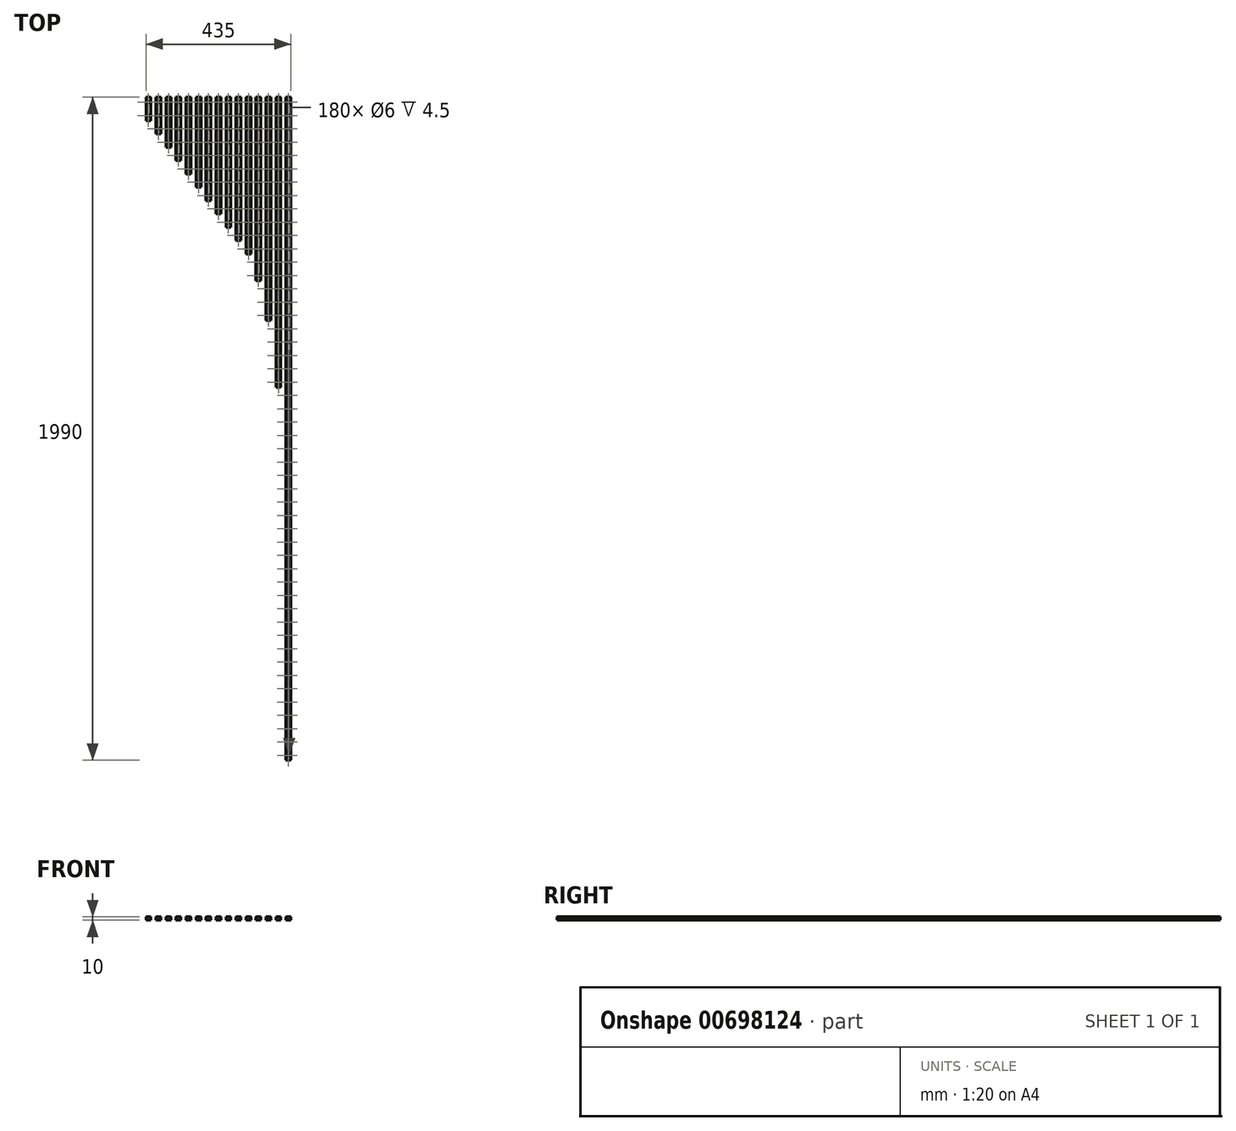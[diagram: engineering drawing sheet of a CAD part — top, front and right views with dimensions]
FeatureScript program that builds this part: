
annotation { "Feature Type Name" : "Feature", "Feature Type Description" : "" }
export const myFeature = defineFeature(function(context is Context, id is Id, definition is map)
    precondition{}
    {
        {
            var Q0;
            Q0=qCreatedBy(makeId("Front.planeOp"),FACE);
            var sketch = newSketch(context, id + "F0", { "sketchPlane" : qUnion([Q0])});
            skPoint(sketch, "E0.middle", {"position": v(0, 0) * mm});
            skLineSegment(sketch, "E1.bottom", {"start": v(6.8, -5) * mm, "end": v(-1.51, -5) * mm});
            skLineSegment(sketch, "E1.top", {"start": v(7, 5) * mm, "end": v(-7, 5) * mm});
            skLineSegment(sketch, "E1.left", {"start": v(7.5, -4.3) * mm, "end": v(7.5, 0.59) * mm});
            skLineSegment(sketch, "E1.right", {"start": v(-7.5, -4.3) * mm, "end": v(-7.5, 0.59) * mm});
            skArc(sketch, "E2", {"start": v(-7.5, 0.59) * mm, "mid": v(-6.98, 0.9) * mm, "end": v(-6.63, 1.4) * mm});
            skArc(sketch, "E3", {"start": v(7.5, 3.41) * mm, "mid": v(6.98, 3.1) * mm, "end": v(6.63, 2.6) * mm});
            skLineSegment(sketch, "E4", {"start": v(5.7, 2.6) * mm, "end": v(6.63, 2.6) * mm});
            skLineSegment(sketch, "E5", {"start": v(5.7, 1.4) * mm, "end": v(6.63, 1.4) * mm});
            skLineSegment(sketch, "E6", {"start": v(-5.7, 1.4) * mm, "end": v(-6.63, 1.4) * mm});
            skLineSegment(sketch, "E7", {"start": v(-5.7, 2.6) * mm, "end": v(-6.63, 2.6) * mm});
            skLineSegment(sketch, "E8", {"start": v(-7.5, 4.5) * mm, "end": v(-7, 5) * mm});
            skLineSegment(sketch, "E9.MirrorCS", {"start": v(7.5, 4.5) * mm, "end": v(7, 5) * mm});
            skLineSegment(sketch, "E10.MirrorCS", {"start": v(7.5, -4.3) * mm, "end": v(6.8, -5) * mm});
            skLineSegment(sketch, "E11.MirrorCS", {"start": v(-7.5, -4.3) * mm, "end": v(-6.8, -5) * mm});
            skPoint(sketch, "E12.orphan", {"position": v(-7.5, 5) * mm});
            skLineSegment(sketch, "E13.trimOffspring", {"start": v(-7.5, 3.41) * mm, "end": v(-7.5, 4.5) * mm});
            skArc(sketch, "E14.trimOffspring", {"start": v(-6.63, 2.6) * mm, "mid": v(-6.98, 3.1) * mm, "end": v(-7.5, 3.41) * mm});
            skPoint(sketch, "E15.orphan", {"position": v(7.5, 5) * mm});
            skLineSegment(sketch, "E16.trimOffspring", {"start": v(7.5, 3.41) * mm, "end": v(7.5, 4.5) * mm});
            skArc(sketch, "E17.trimOffspring", {"start": v(6.63, 1.4) * mm, "mid": v(6.98, 0.9) * mm, "end": v(7.5, 0.59) * mm});
            skPoint(sketch, "E18.orphan", {"position": v(7.5, -5) * mm});
            skPoint(sketch, "E19.orphan", {"position": v(-7.5, -5) * mm});
            skLineSegment(sketch, "E20", {"start": v(-5.7, 2.6) * mm, "end": v(-5.7, 1.4) * mm});
            skLineSegment(sketch, "E21", {"start": v(5.7, 2.6) * mm, "end": v(5.7, 1.4) * mm});
            skLineSegment(sketch, "E22", {"start": v(-8, 2) * mm, "end": v(8, 2) * mm, "construction": true});
            skArc(sketch, "E23", {"start": v(-1.51, -5) * mm, "mid": v(-2, -4.7) * mm, "end": v(-2.49, -5) * mm});
            skLineSegment(sketch, "E24.trimOffspring", {"start": v(-2.49, -5) * mm, "end": v(-6.8, -5) * mm});
            skLineSegment(sketch, "E25", {"start": v(-2.49, -5) * mm, "end": v(-1.51, -5) * mm, "construction": true});
            skLineSegment(sketch, "E26.1.0.0", {"start": v(37, 5) * mm, "end": v(23, 5) * mm});
            skLineSegment(sketch, "E26.1.0.1", {"start": v(36.8, -5) * mm, "end": v(28.49, -5) * mm});
            skArc(sketch, "E26.1.0.2", {"start": v(36.63, 1.4) * mm, "mid": v(36.98, 0.9) * mm, "end": v(37.5, 0.59) * mm});
            skPoint(sketch, "E26.1.0.3", {"position": v(37.5, -5) * mm});
            skPoint(sketch, "E26.1.0.4", {"position": v(22.5, -5) * mm});
            skLineSegment(sketch, "E26.1.0.5", {"start": v(37.5, -4.3) * mm, "end": v(37.5, 0.59) * mm});
            skPoint(sketch, "E26.1.0.6", {"position": v(22.5, 5) * mm});
            skPoint(sketch, "E26.1.0.7", {"position": v(30, 0) * mm});
            skLineSegment(sketch, "E26.1.0.8", {"start": v(22, 2) * mm, "end": v(38, 2) * mm, "construction": true});
            skLineSegment(sketch, "E26.1.0.9", {"start": v(27.51, -5) * mm, "end": v(23.2, -5) * mm});
            skLineSegment(sketch, "E26.1.0.10", {"start": v(22.5, -4.3) * mm, "end": v(22.5, 0.59) * mm});
            skArc(sketch, "E26.1.0.11", {"start": v(22.5, 0.59) * mm, "mid": v(23.02, 0.9) * mm, "end": v(23.37, 1.4) * mm});
            skPoint(sketch, "E26.1.0.12", {"position": v(37.5, 5) * mm});
            skPoint(sketch, "E26.1.0.13", {"position": v(30, 0) * mm});
            skArc(sketch, "E26.1.0.14", {"start": v(36.63, 1.4) * mm, "mid": v(36.98, 0.9) * mm, "end": v(37.5, 0.59) * mm});
            skLineSegment(sketch, "E26.1.0.15", {"start": v(22.5, 3.41) * mm, "end": v(22.5, 4.5) * mm});
            skLineSegment(sketch, "E26.1.0.16", {"start": v(35.7, 2.6) * mm, "end": v(35.7, 1.4) * mm});
            skLineSegment(sketch, "E26.1.0.17", {"start": v(37.5, 4.5) * mm, "end": v(37, 5) * mm});
            skLineSegment(sketch, "E26.1.0.18", {"start": v(37.5, 3.41) * mm, "end": v(37.5, 4.5) * mm});
            skArc(sketch, "E26.1.0.19", {"start": v(23.37, 2.6) * mm, "mid": v(23.02, 3.1) * mm, "end": v(22.5, 3.41) * mm});
            skLineSegment(sketch, "E26.1.0.20", {"start": v(22.5, 4.5) * mm, "end": v(23, 5) * mm});
            skLineSegment(sketch, "E26.1.0.21", {"start": v(22.5, -4.3) * mm, "end": v(23.2, -5) * mm});
            skLineSegment(sketch, "E26.1.0.22", {"start": v(24.3, 2.6) * mm, "end": v(23.37, 2.6) * mm});
            skLineSegment(sketch, "E26.1.0.23", {"start": v(37.5, -4.3) * mm, "end": v(36.8, -5) * mm});
            skLineSegment(sketch, "E26.1.0.24", {"start": v(24.3, 2.6) * mm, "end": v(24.3, 1.4) * mm});
            skArc(sketch, "E26.1.0.25", {"start": v(37.5, 3.41) * mm, "mid": v(36.98, 3.1) * mm, "end": v(36.63, 2.6) * mm});
            skLineSegment(sketch, "E26.1.0.26", {"start": v(35.7, 2.6) * mm, "end": v(36.63, 2.6) * mm});
            skLineSegment(sketch, "E26.1.0.27", {"start": v(35.7, 1.4) * mm, "end": v(36.63, 1.4) * mm});
            skLineSegment(sketch, "E26.1.0.28", {"start": v(24.3, 1.4) * mm, "end": v(23.37, 1.4) * mm});
            skArc(sketch, "E26.1.0.29", {"start": v(28.49, -5) * mm, "mid": v(28, -4.7) * mm, "end": v(27.51, -5) * mm});
            skLineSegment(sketch, "E26.1.0.30", {"start": v(27.51, -5) * mm, "end": v(28.49, -5) * mm, "construction": true});
            skLineSegment(sketch, "E26.2.0.0", {"start": v(67, 5) * mm, "end": v(53, 5) * mm});
            skLineSegment(sketch, "E26.2.0.1", {"start": v(66.8, -5) * mm, "end": v(58.49, -5) * mm});
            skArc(sketch, "E26.2.0.2", {"start": v(66.63, 1.4) * mm, "mid": v(66.98, 0.9) * mm, "end": v(67.5, 0.59) * mm});
            skPoint(sketch, "E26.2.0.3", {"position": v(67.5, -5) * mm});
            skPoint(sketch, "E26.2.0.4", {"position": v(52.5, -5) * mm});
            skLineSegment(sketch, "E26.2.0.5", {"start": v(67.5, -4.3) * mm, "end": v(67.5, 0.59) * mm});
            skPoint(sketch, "E26.2.0.6", {"position": v(52.5, 5) * mm});
            skPoint(sketch, "E26.2.0.7", {"position": v(60, 0) * mm});
            skLineSegment(sketch, "E26.2.0.8", {"start": v(52, 2) * mm, "end": v(68, 2) * mm, "construction": true});
            skLineSegment(sketch, "E26.2.0.9", {"start": v(57.51, -5) * mm, "end": v(53.2, -5) * mm});
            skLineSegment(sketch, "E26.2.0.10", {"start": v(52.5, -4.3) * mm, "end": v(52.5, 0.59) * mm});
            skArc(sketch, "E26.2.0.11", {"start": v(52.5, 0.59) * mm, "mid": v(53.02, 0.9) * mm, "end": v(53.37, 1.4) * mm});
            skPoint(sketch, "E26.2.0.12", {"position": v(67.5, 5) * mm});
            skPoint(sketch, "E26.2.0.13", {"position": v(60, 0) * mm});
            skArc(sketch, "E26.2.0.14", {"start": v(66.63, 1.4) * mm, "mid": v(66.98, 0.9) * mm, "end": v(67.5, 0.59) * mm});
            skLineSegment(sketch, "E26.2.0.15", {"start": v(52.5, 3.41) * mm, "end": v(52.5, 4.5) * mm});
            skLineSegment(sketch, "E26.2.0.16", {"start": v(65.7, 2.6) * mm, "end": v(65.7, 1.4) * mm});
            skLineSegment(sketch, "E26.2.0.17", {"start": v(67.5, 4.5) * mm, "end": v(67, 5) * mm});
            skLineSegment(sketch, "E26.2.0.18", {"start": v(67.5, 3.41) * mm, "end": v(67.5, 4.5) * mm});
            skArc(sketch, "E26.2.0.19", {"start": v(53.37, 2.6) * mm, "mid": v(53.02, 3.1) * mm, "end": v(52.5, 3.41) * mm});
            skLineSegment(sketch, "E26.2.0.20", {"start": v(52.5, 4.5) * mm, "end": v(53, 5) * mm});
            skLineSegment(sketch, "E26.2.0.21", {"start": v(52.5, -4.3) * mm, "end": v(53.2, -5) * mm});
            skLineSegment(sketch, "E26.2.0.22", {"start": v(54.3, 2.6) * mm, "end": v(53.37, 2.6) * mm});
            skLineSegment(sketch, "E26.2.0.23", {"start": v(67.5, -4.3) * mm, "end": v(66.8, -5) * mm});
            skLineSegment(sketch, "E26.2.0.24", {"start": v(54.3, 2.6) * mm, "end": v(54.3, 1.4) * mm});
            skArc(sketch, "E26.2.0.25", {"start": v(67.5, 3.41) * mm, "mid": v(66.98, 3.1) * mm, "end": v(66.63, 2.6) * mm});
            skLineSegment(sketch, "E26.2.0.26", {"start": v(65.7, 2.6) * mm, "end": v(66.63, 2.6) * mm});
            skLineSegment(sketch, "E26.2.0.27", {"start": v(65.7, 1.4) * mm, "end": v(66.63, 1.4) * mm});
            skLineSegment(sketch, "E26.2.0.28", {"start": v(54.3, 1.4) * mm, "end": v(53.37, 1.4) * mm});
            skArc(sketch, "E26.2.0.29", {"start": v(58.49, -5) * mm, "mid": v(58, -4.7) * mm, "end": v(57.51, -5) * mm});
            skLineSegment(sketch, "E26.2.0.30", {"start": v(57.51, -5) * mm, "end": v(58.49, -5) * mm, "construction": true});
            skLineSegment(sketch, "E26.3.0.0", {"start": v(97, 5) * mm, "end": v(83, 5) * mm});
            skLineSegment(sketch, "E26.3.0.1", {"start": v(96.8, -5) * mm, "end": v(88.49, -5) * mm});
            skArc(sketch, "E26.3.0.2", {"start": v(96.63, 1.4) * mm, "mid": v(96.98, 0.9) * mm, "end": v(97.5, 0.59) * mm});
            skPoint(sketch, "E26.3.0.3", {"position": v(97.5, -5) * mm});
            skPoint(sketch, "E26.3.0.4", {"position": v(82.5, -5) * mm});
            skLineSegment(sketch, "E26.3.0.5", {"start": v(97.5, -4.3) * mm, "end": v(97.5, 0.59) * mm});
            skPoint(sketch, "E26.3.0.6", {"position": v(82.5, 5) * mm});
            skPoint(sketch, "E26.3.0.7", {"position": v(90, 0) * mm});
            skLineSegment(sketch, "E26.3.0.8", {"start": v(82, 2) * mm, "end": v(98, 2) * mm, "construction": true});
            skLineSegment(sketch, "E26.3.0.9", {"start": v(87.51, -5) * mm, "end": v(83.2, -5) * mm});
            skLineSegment(sketch, "E26.3.0.10", {"start": v(82.5, -4.3) * mm, "end": v(82.5, 0.59) * mm});
            skArc(sketch, "E26.3.0.11", {"start": v(82.5, 0.59) * mm, "mid": v(83.02, 0.9) * mm, "end": v(83.37, 1.4) * mm});
            skPoint(sketch, "E26.3.0.12", {"position": v(97.5, 5) * mm});
            skPoint(sketch, "E26.3.0.13", {"position": v(90, 0) * mm});
            skArc(sketch, "E26.3.0.14", {"start": v(96.63, 1.4) * mm, "mid": v(96.98, 0.9) * mm, "end": v(97.5, 0.59) * mm});
            skLineSegment(sketch, "E26.3.0.15", {"start": v(82.5, 3.41) * mm, "end": v(82.5, 4.5) * mm});
            skLineSegment(sketch, "E26.3.0.16", {"start": v(95.7, 2.6) * mm, "end": v(95.7, 1.4) * mm});
            skLineSegment(sketch, "E26.3.0.17", {"start": v(97.5, 4.5) * mm, "end": v(97, 5) * mm});
            skLineSegment(sketch, "E26.3.0.18", {"start": v(97.5, 3.41) * mm, "end": v(97.5, 4.5) * mm});
            skArc(sketch, "E26.3.0.19", {"start": v(83.37, 2.6) * mm, "mid": v(83.02, 3.1) * mm, "end": v(82.5, 3.41) * mm});
            skLineSegment(sketch, "E26.3.0.20", {"start": v(82.5, 4.5) * mm, "end": v(83, 5) * mm});
            skLineSegment(sketch, "E26.3.0.21", {"start": v(82.5, -4.3) * mm, "end": v(83.2, -5) * mm});
            skLineSegment(sketch, "E26.3.0.22", {"start": v(84.3, 2.6) * mm, "end": v(83.37, 2.6) * mm});
            skLineSegment(sketch, "E26.3.0.23", {"start": v(97.5, -4.3) * mm, "end": v(96.8, -5) * mm});
            skLineSegment(sketch, "E26.3.0.24", {"start": v(84.3, 2.6) * mm, "end": v(84.3, 1.4) * mm});
            skArc(sketch, "E26.3.0.25", {"start": v(97.5, 3.41) * mm, "mid": v(96.98, 3.1) * mm, "end": v(96.63, 2.6) * mm});
            skLineSegment(sketch, "E26.3.0.26", {"start": v(95.7, 2.6) * mm, "end": v(96.63, 2.6) * mm});
            skLineSegment(sketch, "E26.3.0.27", {"start": v(95.7, 1.4) * mm, "end": v(96.63, 1.4) * mm});
            skLineSegment(sketch, "E26.3.0.28", {"start": v(84.3, 1.4) * mm, "end": v(83.37, 1.4) * mm});
            skArc(sketch, "E26.3.0.29", {"start": v(88.49, -5) * mm, "mid": v(88, -4.7) * mm, "end": v(87.51, -5) * mm});
            skLineSegment(sketch, "E26.3.0.30", {"start": v(87.51, -5) * mm, "end": v(88.49, -5) * mm, "construction": true});
            skLineSegment(sketch, "E26.4.0.0", {"start": v(127, 5) * mm, "end": v(113, 5) * mm});
            skLineSegment(sketch, "E26.4.0.1", {"start": v(126.8, -5) * mm, "end": v(118.49, -5) * mm});
            skArc(sketch, "E26.4.0.2", {"start": v(126.63, 1.4) * mm, "mid": v(126.98, 0.9) * mm, "end": v(127.5, 0.59) * mm});
            skPoint(sketch, "E26.4.0.3", {"position": v(127.5, -5) * mm});
            skPoint(sketch, "E26.4.0.4", {"position": v(112.5, -5) * mm});
            skLineSegment(sketch, "E26.4.0.5", {"start": v(127.5, -4.3) * mm, "end": v(127.5, 0.59) * mm});
            skPoint(sketch, "E26.4.0.6", {"position": v(112.5, 5) * mm});
            skPoint(sketch, "E26.4.0.7", {"position": v(120, 0) * mm});
            skLineSegment(sketch, "E26.4.0.8", {"start": v(112, 2) * mm, "end": v(128, 2) * mm, "construction": true});
            skLineSegment(sketch, "E26.4.0.9", {"start": v(117.51, -5) * mm, "end": v(113.2, -5) * mm});
            skLineSegment(sketch, "E26.4.0.10", {"start": v(112.5, -4.3) * mm, "end": v(112.5, 0.59) * mm});
            skArc(sketch, "E26.4.0.11", {"start": v(112.5, 0.59) * mm, "mid": v(113.02, 0.9) * mm, "end": v(113.37, 1.4) * mm});
            skPoint(sketch, "E26.4.0.12", {"position": v(127.5, 5) * mm});
            skPoint(sketch, "E26.4.0.13", {"position": v(120, 0) * mm});
            skArc(sketch, "E26.4.0.14", {"start": v(126.63, 1.4) * mm, "mid": v(126.98, 0.9) * mm, "end": v(127.5, 0.59) * mm});
            skLineSegment(sketch, "E26.4.0.15", {"start": v(112.5, 3.41) * mm, "end": v(112.5, 4.5) * mm});
            skLineSegment(sketch, "E26.4.0.16", {"start": v(125.7, 2.6) * mm, "end": v(125.7, 1.4) * mm});
            skLineSegment(sketch, "E26.4.0.17", {"start": v(127.5, 4.5) * mm, "end": v(127, 5) * mm});
            skLineSegment(sketch, "E26.4.0.18", {"start": v(127.5, 3.41) * mm, "end": v(127.5, 4.5) * mm});
            skArc(sketch, "E26.4.0.19", {"start": v(113.37, 2.6) * mm, "mid": v(113.02, 3.1) * mm, "end": v(112.5, 3.41) * mm});
            skLineSegment(sketch, "E26.4.0.20", {"start": v(112.5, 4.5) * mm, "end": v(113, 5) * mm});
            skLineSegment(sketch, "E26.4.0.21", {"start": v(112.5, -4.3) * mm, "end": v(113.2, -5) * mm});
            skLineSegment(sketch, "E26.4.0.22", {"start": v(114.3, 2.6) * mm, "end": v(113.37, 2.6) * mm});
            skLineSegment(sketch, "E26.4.0.23", {"start": v(127.5, -4.3) * mm, "end": v(126.8, -5) * mm});
            skLineSegment(sketch, "E26.4.0.24", {"start": v(114.3, 2.6) * mm, "end": v(114.3, 1.4) * mm});
            skArc(sketch, "E26.4.0.25", {"start": v(127.5, 3.41) * mm, "mid": v(126.98, 3.1) * mm, "end": v(126.63, 2.6) * mm});
            skLineSegment(sketch, "E26.4.0.26", {"start": v(125.7, 2.6) * mm, "end": v(126.63, 2.6) * mm});
            skLineSegment(sketch, "E26.4.0.27", {"start": v(125.7, 1.4) * mm, "end": v(126.63, 1.4) * mm});
            skLineSegment(sketch, "E26.4.0.28", {"start": v(114.3, 1.4) * mm, "end": v(113.37, 1.4) * mm});
            skArc(sketch, "E26.4.0.29", {"start": v(118.49, -5) * mm, "mid": v(118, -4.7) * mm, "end": v(117.51, -5) * mm});
            skLineSegment(sketch, "E26.4.0.30", {"start": v(117.51, -5) * mm, "end": v(118.49, -5) * mm, "construction": true});
            skLineSegment(sketch, "E26.5.0.0", {"start": v(157, 5) * mm, "end": v(143, 5) * mm});
            skLineSegment(sketch, "E26.5.0.1", {"start": v(156.8, -5) * mm, "end": v(148.49, -5) * mm});
            skArc(sketch, "E26.5.0.2", {"start": v(156.63, 1.4) * mm, "mid": v(156.98, 0.9) * mm, "end": v(157.5, 0.59) * mm});
            skPoint(sketch, "E26.5.0.3", {"position": v(157.5, -5) * mm});
            skPoint(sketch, "E26.5.0.4", {"position": v(142.5, -5) * mm});
            skLineSegment(sketch, "E26.5.0.5", {"start": v(157.5, -4.3) * mm, "end": v(157.5, 0.59) * mm});
            skPoint(sketch, "E26.5.0.6", {"position": v(142.5, 5) * mm});
            skPoint(sketch, "E26.5.0.7", {"position": v(150, 0) * mm});
            skLineSegment(sketch, "E26.5.0.8", {"start": v(142, 2) * mm, "end": v(158, 2) * mm, "construction": true});
            skLineSegment(sketch, "E26.5.0.9", {"start": v(147.51, -5) * mm, "end": v(143.2, -5) * mm});
            skLineSegment(sketch, "E26.5.0.10", {"start": v(142.5, -4.3) * mm, "end": v(142.5, 0.59) * mm});
            skArc(sketch, "E26.5.0.11", {"start": v(142.5, 0.59) * mm, "mid": v(143.02, 0.9) * mm, "end": v(143.37, 1.4) * mm});
            skPoint(sketch, "E26.5.0.12", {"position": v(157.5, 5) * mm});
            skPoint(sketch, "E26.5.0.13", {"position": v(150, 0) * mm});
            skArc(sketch, "E26.5.0.14", {"start": v(156.63, 1.4) * mm, "mid": v(156.98, 0.9) * mm, "end": v(157.5, 0.59) * mm});
            skLineSegment(sketch, "E26.5.0.15", {"start": v(142.5, 3.41) * mm, "end": v(142.5, 4.5) * mm});
            skLineSegment(sketch, "E26.5.0.16", {"start": v(155.7, 2.6) * mm, "end": v(155.7, 1.4) * mm});
            skLineSegment(sketch, "E26.5.0.17", {"start": v(157.5, 4.5) * mm, "end": v(157, 5) * mm});
            skLineSegment(sketch, "E26.5.0.18", {"start": v(157.5, 3.41) * mm, "end": v(157.5, 4.5) * mm});
            skArc(sketch, "E26.5.0.19", {"start": v(143.37, 2.6) * mm, "mid": v(143.02, 3.1) * mm, "end": v(142.5, 3.41) * mm});
            skLineSegment(sketch, "E26.5.0.20", {"start": v(142.5, 4.5) * mm, "end": v(143, 5) * mm});
            skLineSegment(sketch, "E26.5.0.21", {"start": v(142.5, -4.3) * mm, "end": v(143.2, -5) * mm});
            skLineSegment(sketch, "E26.5.0.22", {"start": v(144.3, 2.6) * mm, "end": v(143.37, 2.6) * mm});
            skLineSegment(sketch, "E26.5.0.23", {"start": v(157.5, -4.3) * mm, "end": v(156.8, -5) * mm});
            skLineSegment(sketch, "E26.5.0.24", {"start": v(144.3, 2.6) * mm, "end": v(144.3, 1.4) * mm});
            skArc(sketch, "E26.5.0.25", {"start": v(157.5, 3.41) * mm, "mid": v(156.98, 3.1) * mm, "end": v(156.63, 2.6) * mm});
            skLineSegment(sketch, "E26.5.0.26", {"start": v(155.7, 2.6) * mm, "end": v(156.63, 2.6) * mm});
            skLineSegment(sketch, "E26.5.0.27", {"start": v(155.7, 1.4) * mm, "end": v(156.63, 1.4) * mm});
            skLineSegment(sketch, "E26.5.0.28", {"start": v(144.3, 1.4) * mm, "end": v(143.37, 1.4) * mm});
            skArc(sketch, "E26.5.0.29", {"start": v(148.49, -5) * mm, "mid": v(148, -4.7) * mm, "end": v(147.51, -5) * mm});
            skLineSegment(sketch, "E26.5.0.30", {"start": v(147.51, -5) * mm, "end": v(148.49, -5) * mm, "construction": true});
            skLineSegment(sketch, "E26.6.0.0", {"start": v(187, 5) * mm, "end": v(173, 5) * mm});
            skLineSegment(sketch, "E26.6.0.1", {"start": v(186.8, -5) * mm, "end": v(178.49, -5) * mm});
            skArc(sketch, "E26.6.0.2", {"start": v(186.63, 1.4) * mm, "mid": v(186.98, 0.9) * mm, "end": v(187.5, 0.59) * mm});
            skPoint(sketch, "E26.6.0.3", {"position": v(187.5, -5) * mm});
            skPoint(sketch, "E26.6.0.4", {"position": v(172.5, -5) * mm});
            skLineSegment(sketch, "E26.6.0.5", {"start": v(187.5, -4.3) * mm, "end": v(187.5, 0.59) * mm});
            skPoint(sketch, "E26.6.0.6", {"position": v(172.5, 5) * mm});
            skPoint(sketch, "E26.6.0.7", {"position": v(180, 0) * mm});
            skLineSegment(sketch, "E26.6.0.8", {"start": v(172, 2) * mm, "end": v(188, 2) * mm, "construction": true});
            skLineSegment(sketch, "E26.6.0.9", {"start": v(177.51, -5) * mm, "end": v(173.2, -5) * mm});
            skLineSegment(sketch, "E26.6.0.10", {"start": v(172.5, -4.3) * mm, "end": v(172.5, 0.59) * mm});
            skArc(sketch, "E26.6.0.11", {"start": v(172.5, 0.59) * mm, "mid": v(173.02, 0.9) * mm, "end": v(173.37, 1.4) * mm});
            skPoint(sketch, "E26.6.0.12", {"position": v(187.5, 5) * mm});
            skPoint(sketch, "E26.6.0.13", {"position": v(180, 0) * mm});
            skArc(sketch, "E26.6.0.14", {"start": v(186.63, 1.4) * mm, "mid": v(186.98, 0.9) * mm, "end": v(187.5, 0.59) * mm});
            skLineSegment(sketch, "E26.6.0.15", {"start": v(172.5, 3.41) * mm, "end": v(172.5, 4.5) * mm});
            skLineSegment(sketch, "E26.6.0.16", {"start": v(185.7, 2.6) * mm, "end": v(185.7, 1.4) * mm});
            skLineSegment(sketch, "E26.6.0.17", {"start": v(187.5, 4.5) * mm, "end": v(187, 5) * mm});
            skLineSegment(sketch, "E26.6.0.18", {"start": v(187.5, 3.41) * mm, "end": v(187.5, 4.5) * mm});
            skArc(sketch, "E26.6.0.19", {"start": v(173.37, 2.6) * mm, "mid": v(173.02, 3.1) * mm, "end": v(172.5, 3.41) * mm});
            skLineSegment(sketch, "E26.6.0.20", {"start": v(172.5, 4.5) * mm, "end": v(173, 5) * mm});
            skLineSegment(sketch, "E26.6.0.21", {"start": v(172.5, -4.3) * mm, "end": v(173.2, -5) * mm});
            skLineSegment(sketch, "E26.6.0.22", {"start": v(174.3, 2.6) * mm, "end": v(173.37, 2.6) * mm});
            skLineSegment(sketch, "E26.6.0.23", {"start": v(187.5, -4.3) * mm, "end": v(186.8, -5) * mm});
            skLineSegment(sketch, "E26.6.0.24", {"start": v(174.3, 2.6) * mm, "end": v(174.3, 1.4) * mm});
            skArc(sketch, "E26.6.0.25", {"start": v(187.5, 3.41) * mm, "mid": v(186.98, 3.1) * mm, "end": v(186.63, 2.6) * mm});
            skLineSegment(sketch, "E26.6.0.26", {"start": v(185.7, 2.6) * mm, "end": v(186.63, 2.6) * mm});
            skLineSegment(sketch, "E26.6.0.27", {"start": v(185.7, 1.4) * mm, "end": v(186.63, 1.4) * mm});
            skLineSegment(sketch, "E26.6.0.28", {"start": v(174.3, 1.4) * mm, "end": v(173.37, 1.4) * mm});
            skArc(sketch, "E26.6.0.29", {"start": v(178.49, -5) * mm, "mid": v(178, -4.7) * mm, "end": v(177.51, -5) * mm});
            skLineSegment(sketch, "E26.6.0.30", {"start": v(177.51, -5) * mm, "end": v(178.49, -5) * mm, "construction": true});
            skLineSegment(sketch, "E26.7.0.0", {"start": v(217, 5) * mm, "end": v(203, 5) * mm});
            skLineSegment(sketch, "E26.7.0.1", {"start": v(216.8, -5) * mm, "end": v(208.49, -5) * mm});
            skArc(sketch, "E26.7.0.2", {"start": v(216.63, 1.4) * mm, "mid": v(216.98, 0.9) * mm, "end": v(217.5, 0.59) * mm});
            skPoint(sketch, "E26.7.0.3", {"position": v(217.5, -5) * mm});
            skPoint(sketch, "E26.7.0.4", {"position": v(202.5, -5) * mm});
            skLineSegment(sketch, "E26.7.0.5", {"start": v(217.5, -4.3) * mm, "end": v(217.5, 0.59) * mm});
            skPoint(sketch, "E26.7.0.6", {"position": v(202.5, 5) * mm});
            skPoint(sketch, "E26.7.0.7", {"position": v(210, 0) * mm});
            skLineSegment(sketch, "E26.7.0.8", {"start": v(202, 2) * mm, "end": v(218, 2) * mm, "construction": true});
            skLineSegment(sketch, "E26.7.0.9", {"start": v(207.51, -5) * mm, "end": v(203.2, -5) * mm});
            skLineSegment(sketch, "E26.7.0.10", {"start": v(202.5, -4.3) * mm, "end": v(202.5, 0.59) * mm});
            skArc(sketch, "E26.7.0.11", {"start": v(202.5, 0.59) * mm, "mid": v(203.02, 0.9) * mm, "end": v(203.37, 1.4) * mm});
            skPoint(sketch, "E26.7.0.12", {"position": v(217.5, 5) * mm});
            skPoint(sketch, "E26.7.0.13", {"position": v(210, 0) * mm});
            skArc(sketch, "E26.7.0.14", {"start": v(216.63, 1.4) * mm, "mid": v(216.98, 0.9) * mm, "end": v(217.5, 0.59) * mm});
            skLineSegment(sketch, "E26.7.0.15", {"start": v(202.5, 3.41) * mm, "end": v(202.5, 4.5) * mm});
            skLineSegment(sketch, "E26.7.0.16", {"start": v(215.7, 2.6) * mm, "end": v(215.7, 1.4) * mm});
            skLineSegment(sketch, "E26.7.0.17", {"start": v(217.5, 4.5) * mm, "end": v(217, 5) * mm});
            skLineSegment(sketch, "E26.7.0.18", {"start": v(217.5, 3.41) * mm, "end": v(217.5, 4.5) * mm});
            skArc(sketch, "E26.7.0.19", {"start": v(203.37, 2.6) * mm, "mid": v(203.02, 3.1) * mm, "end": v(202.5, 3.41) * mm});
            skLineSegment(sketch, "E26.7.0.20", {"start": v(202.5, 4.5) * mm, "end": v(203, 5) * mm});
            skLineSegment(sketch, "E26.7.0.21", {"start": v(202.5, -4.3) * mm, "end": v(203.2, -5) * mm});
            skLineSegment(sketch, "E26.7.0.22", {"start": v(204.3, 2.6) * mm, "end": v(203.37, 2.6) * mm});
            skLineSegment(sketch, "E26.7.0.23", {"start": v(217.5, -4.3) * mm, "end": v(216.8, -5) * mm});
            skLineSegment(sketch, "E26.7.0.24", {"start": v(204.3, 2.6) * mm, "end": v(204.3, 1.4) * mm});
            skArc(sketch, "E26.7.0.25", {"start": v(217.5, 3.41) * mm, "mid": v(216.98, 3.1) * mm, "end": v(216.63, 2.6) * mm});
            skLineSegment(sketch, "E26.7.0.26", {"start": v(215.7, 2.6) * mm, "end": v(216.63, 2.6) * mm});
            skLineSegment(sketch, "E26.7.0.27", {"start": v(215.7, 1.4) * mm, "end": v(216.63, 1.4) * mm});
            skLineSegment(sketch, "E26.7.0.28", {"start": v(204.3, 1.4) * mm, "end": v(203.37, 1.4) * mm});
            skArc(sketch, "E26.7.0.29", {"start": v(208.49, -5) * mm, "mid": v(208, -4.7) * mm, "end": v(207.51, -5) * mm});
            skLineSegment(sketch, "E26.7.0.30", {"start": v(207.51, -5) * mm, "end": v(208.49, -5) * mm, "construction": true});
            skLineSegment(sketch, "E26.8.0.0", {"start": v(247, 5) * mm, "end": v(233, 5) * mm});
            skLineSegment(sketch, "E26.8.0.1", {"start": v(246.8, -5) * mm, "end": v(238.49, -5) * mm});
            skArc(sketch, "E26.8.0.2", {"start": v(246.63, 1.4) * mm, "mid": v(246.98, 0.9) * mm, "end": v(247.5, 0.59) * mm});
            skPoint(sketch, "E26.8.0.3", {"position": v(247.5, -5) * mm});
            skPoint(sketch, "E26.8.0.4", {"position": v(232.5, -5) * mm});
            skLineSegment(sketch, "E26.8.0.5", {"start": v(247.5, -4.3) * mm, "end": v(247.5, 0.59) * mm});
            skPoint(sketch, "E26.8.0.6", {"position": v(232.5, 5) * mm});
            skPoint(sketch, "E26.8.0.7", {"position": v(240, 0) * mm});
            skLineSegment(sketch, "E26.8.0.8", {"start": v(232, 2) * mm, "end": v(248, 2) * mm, "construction": true});
            skLineSegment(sketch, "E26.8.0.9", {"start": v(237.51, -5) * mm, "end": v(233.2, -5) * mm});
            skLineSegment(sketch, "E26.8.0.10", {"start": v(232.5, -4.3) * mm, "end": v(232.5, 0.59) * mm});
            skArc(sketch, "E26.8.0.11", {"start": v(232.5, 0.59) * mm, "mid": v(233.02, 0.9) * mm, "end": v(233.37, 1.4) * mm});
            skPoint(sketch, "E26.8.0.12", {"position": v(247.5, 5) * mm});
            skPoint(sketch, "E26.8.0.13", {"position": v(240, 0) * mm});
            skArc(sketch, "E26.8.0.14", {"start": v(246.63, 1.4) * mm, "mid": v(246.98, 0.9) * mm, "end": v(247.5, 0.59) * mm});
            skLineSegment(sketch, "E26.8.0.15", {"start": v(232.5, 3.41) * mm, "end": v(232.5, 4.5) * mm});
            skLineSegment(sketch, "E26.8.0.16", {"start": v(245.7, 2.6) * mm, "end": v(245.7, 1.4) * mm});
            skLineSegment(sketch, "E26.8.0.17", {"start": v(247.5, 4.5) * mm, "end": v(247, 5) * mm});
            skLineSegment(sketch, "E26.8.0.18", {"start": v(247.5, 3.41) * mm, "end": v(247.5, 4.5) * mm});
            skArc(sketch, "E26.8.0.19", {"start": v(233.37, 2.6) * mm, "mid": v(233.02, 3.1) * mm, "end": v(232.5, 3.41) * mm});
            skLineSegment(sketch, "E26.8.0.20", {"start": v(232.5, 4.5) * mm, "end": v(233, 5) * mm});
            skLineSegment(sketch, "E26.8.0.21", {"start": v(232.5, -4.3) * mm, "end": v(233.2, -5) * mm});
            skLineSegment(sketch, "E26.8.0.22", {"start": v(234.3, 2.6) * mm, "end": v(233.37, 2.6) * mm});
            skLineSegment(sketch, "E26.8.0.23", {"start": v(247.5, -4.3) * mm, "end": v(246.8, -5) * mm});
            skLineSegment(sketch, "E26.8.0.24", {"start": v(234.3, 2.6) * mm, "end": v(234.3, 1.4) * mm});
            skArc(sketch, "E26.8.0.25", {"start": v(247.5, 3.41) * mm, "mid": v(246.98, 3.1) * mm, "end": v(246.63, 2.6) * mm});
            skLineSegment(sketch, "E26.8.0.26", {"start": v(245.7, 2.6) * mm, "end": v(246.63, 2.6) * mm});
            skLineSegment(sketch, "E26.8.0.27", {"start": v(245.7, 1.4) * mm, "end": v(246.63, 1.4) * mm});
            skLineSegment(sketch, "E26.8.0.28", {"start": v(234.3, 1.4) * mm, "end": v(233.37, 1.4) * mm});
            skArc(sketch, "E26.8.0.29", {"start": v(238.49, -5) * mm, "mid": v(238, -4.7) * mm, "end": v(237.51, -5) * mm});
            skLineSegment(sketch, "E26.8.0.30", {"start": v(237.51, -5) * mm, "end": v(238.49, -5) * mm, "construction": true});
            skLineSegment(sketch, "E26.9.0.0", {"start": v(277, 5) * mm, "end": v(263, 5) * mm});
            skLineSegment(sketch, "E26.9.0.1", {"start": v(276.8, -5) * mm, "end": v(268.49, -5) * mm});
            skArc(sketch, "E26.9.0.2", {"start": v(276.63, 1.4) * mm, "mid": v(276.98, 0.9) * mm, "end": v(277.5, 0.59) * mm});
            skPoint(sketch, "E26.9.0.3", {"position": v(277.5, -5) * mm});
            skPoint(sketch, "E26.9.0.4", {"position": v(262.5, -5) * mm});
            skLineSegment(sketch, "E26.9.0.5", {"start": v(277.5, -4.3) * mm, "end": v(277.5, 0.59) * mm});
            skPoint(sketch, "E26.9.0.6", {"position": v(262.5, 5) * mm});
            skPoint(sketch, "E26.9.0.7", {"position": v(270, 0) * mm});
            skLineSegment(sketch, "E26.9.0.8", {"start": v(262, 2) * mm, "end": v(278, 2) * mm, "construction": true});
            skLineSegment(sketch, "E26.9.0.9", {"start": v(267.51, -5) * mm, "end": v(263.2, -5) * mm});
            skLineSegment(sketch, "E26.9.0.10", {"start": v(262.5, -4.3) * mm, "end": v(262.5, 0.59) * mm});
            skArc(sketch, "E26.9.0.11", {"start": v(262.5, 0.59) * mm, "mid": v(263.02, 0.9) * mm, "end": v(263.37, 1.4) * mm});
            skPoint(sketch, "E26.9.0.12", {"position": v(277.5, 5) * mm});
            skPoint(sketch, "E26.9.0.13", {"position": v(270, 0) * mm});
            skArc(sketch, "E26.9.0.14", {"start": v(276.63, 1.4) * mm, "mid": v(276.98, 0.9) * mm, "end": v(277.5, 0.59) * mm});
            skLineSegment(sketch, "E26.9.0.15", {"start": v(262.5, 3.41) * mm, "end": v(262.5, 4.5) * mm});
            skLineSegment(sketch, "E26.9.0.16", {"start": v(275.7, 2.6) * mm, "end": v(275.7, 1.4) * mm});
            skLineSegment(sketch, "E26.9.0.17", {"start": v(277.5, 4.5) * mm, "end": v(277, 5) * mm});
            skLineSegment(sketch, "E26.9.0.18", {"start": v(277.5, 3.41) * mm, "end": v(277.5, 4.5) * mm});
            skArc(sketch, "E26.9.0.19", {"start": v(263.37, 2.6) * mm, "mid": v(263.02, 3.1) * mm, "end": v(262.5, 3.41) * mm});
            skLineSegment(sketch, "E26.9.0.20", {"start": v(262.5, 4.5) * mm, "end": v(263, 5) * mm});
            skLineSegment(sketch, "E26.9.0.21", {"start": v(262.5, -4.3) * mm, "end": v(263.2, -5) * mm});
            skLineSegment(sketch, "E26.9.0.22", {"start": v(264.3, 2.6) * mm, "end": v(263.37, 2.6) * mm});
            skLineSegment(sketch, "E26.9.0.23", {"start": v(277.5, -4.3) * mm, "end": v(276.8, -5) * mm});
            skLineSegment(sketch, "E26.9.0.24", {"start": v(264.3, 2.6) * mm, "end": v(264.3, 1.4) * mm});
            skArc(sketch, "E26.9.0.25", {"start": v(277.5, 3.41) * mm, "mid": v(276.98, 3.1) * mm, "end": v(276.63, 2.6) * mm});
            skLineSegment(sketch, "E26.9.0.26", {"start": v(275.7, 2.6) * mm, "end": v(276.63, 2.6) * mm});
            skLineSegment(sketch, "E26.9.0.27", {"start": v(275.7, 1.4) * mm, "end": v(276.63, 1.4) * mm});
            skLineSegment(sketch, "E26.9.0.28", {"start": v(264.3, 1.4) * mm, "end": v(263.37, 1.4) * mm});
            skArc(sketch, "E26.9.0.29", {"start": v(268.49, -5) * mm, "mid": v(268, -4.7) * mm, "end": v(267.51, -5) * mm});
            skLineSegment(sketch, "E26.9.0.30", {"start": v(267.51, -5) * mm, "end": v(268.49, -5) * mm, "construction": true});
            skLineSegment(sketch, "E26.10.0.0", {"start": v(307, 5) * mm, "end": v(293, 5) * mm});
            skLineSegment(sketch, "E26.10.0.1", {"start": v(306.8, -5) * mm, "end": v(298.49, -5) * mm});
            skArc(sketch, "E26.10.0.2", {"start": v(306.63, 1.4) * mm, "mid": v(306.98, 0.9) * mm, "end": v(307.5, 0.59) * mm});
            skPoint(sketch, "E26.10.0.3", {"position": v(307.5, -5) * mm});
            skPoint(sketch, "E26.10.0.4", {"position": v(292.5, -5) * mm});
            skLineSegment(sketch, "E26.10.0.5", {"start": v(307.5, -4.3) * mm, "end": v(307.5, 0.59) * mm});
            skPoint(sketch, "E26.10.0.6", {"position": v(292.5, 5) * mm});
            skPoint(sketch, "E26.10.0.7", {"position": v(300, 0) * mm});
            skLineSegment(sketch, "E26.10.0.8", {"start": v(292, 2) * mm, "end": v(308, 2) * mm, "construction": true});
            skLineSegment(sketch, "E26.10.0.9", {"start": v(297.51, -5) * mm, "end": v(293.2, -5) * mm});
            skLineSegment(sketch, "E26.10.0.10", {"start": v(292.5, -4.3) * mm, "end": v(292.5, 0.59) * mm});
            skArc(sketch, "E26.10.0.11", {"start": v(292.5, 0.59) * mm, "mid": v(293.02, 0.9) * mm, "end": v(293.37, 1.4) * mm});
            skPoint(sketch, "E26.10.0.12", {"position": v(307.5, 5) * mm});
            skPoint(sketch, "E26.10.0.13", {"position": v(300, 0) * mm});
            skArc(sketch, "E26.10.0.14", {"start": v(306.63, 1.4) * mm, "mid": v(306.98, 0.9) * mm, "end": v(307.5, 0.59) * mm});
            skLineSegment(sketch, "E26.10.0.15", {"start": v(292.5, 3.41) * mm, "end": v(292.5, 4.5) * mm});
            skLineSegment(sketch, "E26.10.0.16", {"start": v(305.7, 2.6) * mm, "end": v(305.7, 1.4) * mm});
            skLineSegment(sketch, "E26.10.0.17", {"start": v(307.5, 4.5) * mm, "end": v(307, 5) * mm});
            skLineSegment(sketch, "E26.10.0.18", {"start": v(307.5, 3.41) * mm, "end": v(307.5, 4.5) * mm});
            skArc(sketch, "E26.10.0.19", {"start": v(293.37, 2.6) * mm, "mid": v(293.02, 3.1) * mm, "end": v(292.5, 3.41) * mm});
            skLineSegment(sketch, "E26.10.0.20", {"start": v(292.5, 4.5) * mm, "end": v(293, 5) * mm});
            skLineSegment(sketch, "E26.10.0.21", {"start": v(292.5, -4.3) * mm, "end": v(293.2, -5) * mm});
            skLineSegment(sketch, "E26.10.0.22", {"start": v(294.3, 2.6) * mm, "end": v(293.37, 2.6) * mm});
            skLineSegment(sketch, "E26.10.0.23", {"start": v(307.5, -4.3) * mm, "end": v(306.8, -5) * mm});
            skLineSegment(sketch, "E26.10.0.24", {"start": v(294.3, 2.6) * mm, "end": v(294.3, 1.4) * mm});
            skArc(sketch, "E26.10.0.25", {"start": v(307.5, 3.41) * mm, "mid": v(306.98, 3.1) * mm, "end": v(306.63, 2.6) * mm});
            skLineSegment(sketch, "E26.10.0.26", {"start": v(305.7, 2.6) * mm, "end": v(306.63, 2.6) * mm});
            skLineSegment(sketch, "E26.10.0.27", {"start": v(305.7, 1.4) * mm, "end": v(306.63, 1.4) * mm});
            skLineSegment(sketch, "E26.10.0.28", {"start": v(294.3, 1.4) * mm, "end": v(293.37, 1.4) * mm});
            skArc(sketch, "E26.10.0.29", {"start": v(298.49, -5) * mm, "mid": v(298, -4.7) * mm, "end": v(297.51, -5) * mm});
            skLineSegment(sketch, "E26.10.0.30", {"start": v(297.51, -5) * mm, "end": v(298.49, -5) * mm, "construction": true});
            skLineSegment(sketch, "E26.11.0.0", {"start": v(337, 5) * mm, "end": v(323, 5) * mm});
            skLineSegment(sketch, "E26.11.0.1", {"start": v(336.8, -5) * mm, "end": v(328.49, -5) * mm});
            skArc(sketch, "E26.11.0.2", {"start": v(336.63, 1.4) * mm, "mid": v(336.98, 0.9) * mm, "end": v(337.5, 0.59) * mm});
            skPoint(sketch, "E26.11.0.3", {"position": v(337.5, -5) * mm});
            skPoint(sketch, "E26.11.0.4", {"position": v(322.5, -5) * mm});
            skLineSegment(sketch, "E26.11.0.5", {"start": v(337.5, -4.3) * mm, "end": v(337.5, 0.59) * mm});
            skPoint(sketch, "E26.11.0.6", {"position": v(322.5, 5) * mm});
            skPoint(sketch, "E26.11.0.7", {"position": v(330, 0) * mm});
            skLineSegment(sketch, "E26.11.0.8", {"start": v(322, 2) * mm, "end": v(338, 2) * mm, "construction": true});
            skLineSegment(sketch, "E26.11.0.9", {"start": v(327.51, -5) * mm, "end": v(323.2, -5) * mm});
            skLineSegment(sketch, "E26.11.0.10", {"start": v(322.5, -4.3) * mm, "end": v(322.5, 0.59) * mm});
            skArc(sketch, "E26.11.0.11", {"start": v(322.5, 0.59) * mm, "mid": v(323.02, 0.9) * mm, "end": v(323.37, 1.4) * mm});
            skPoint(sketch, "E26.11.0.12", {"position": v(337.5, 5) * mm});
            skPoint(sketch, "E26.11.0.13", {"position": v(330, 0) * mm});
            skArc(sketch, "E26.11.0.14", {"start": v(336.63, 1.4) * mm, "mid": v(336.98, 0.9) * mm, "end": v(337.5, 0.59) * mm});
            skLineSegment(sketch, "E26.11.0.15", {"start": v(322.5, 3.41) * mm, "end": v(322.5, 4.5) * mm});
            skLineSegment(sketch, "E26.11.0.16", {"start": v(335.7, 2.6) * mm, "end": v(335.7, 1.4) * mm});
            skLineSegment(sketch, "E26.11.0.17", {"start": v(337.5, 4.5) * mm, "end": v(337, 5) * mm});
            skLineSegment(sketch, "E26.11.0.18", {"start": v(337.5, 3.41) * mm, "end": v(337.5, 4.5) * mm});
            skArc(sketch, "E26.11.0.19", {"start": v(323.37, 2.6) * mm, "mid": v(323.02, 3.1) * mm, "end": v(322.5, 3.41) * mm});
            skLineSegment(sketch, "E26.11.0.20", {"start": v(322.5, 4.5) * mm, "end": v(323, 5) * mm});
            skLineSegment(sketch, "E26.11.0.21", {"start": v(322.5, -4.3) * mm, "end": v(323.2, -5) * mm});
            skLineSegment(sketch, "E26.11.0.22", {"start": v(324.3, 2.6) * mm, "end": v(323.37, 2.6) * mm});
            skLineSegment(sketch, "E26.11.0.23", {"start": v(337.5, -4.3) * mm, "end": v(336.8, -5) * mm});
            skLineSegment(sketch, "E26.11.0.24", {"start": v(324.3, 2.6) * mm, "end": v(324.3, 1.4) * mm});
            skArc(sketch, "E26.11.0.25", {"start": v(337.5, 3.41) * mm, "mid": v(336.98, 3.1) * mm, "end": v(336.63, 2.6) * mm});
            skLineSegment(sketch, "E26.11.0.26", {"start": v(335.7, 2.6) * mm, "end": v(336.63, 2.6) * mm});
            skLineSegment(sketch, "E26.11.0.27", {"start": v(335.7, 1.4) * mm, "end": v(336.63, 1.4) * mm});
            skLineSegment(sketch, "E26.11.0.28", {"start": v(324.3, 1.4) * mm, "end": v(323.37, 1.4) * mm});
            skArc(sketch, "E26.11.0.29", {"start": v(328.49, -5) * mm, "mid": v(328, -4.7) * mm, "end": v(327.51, -5) * mm});
            skLineSegment(sketch, "E26.11.0.30", {"start": v(327.51, -5) * mm, "end": v(328.49, -5) * mm, "construction": true});
            skLineSegment(sketch, "E26.12.0.0", {"start": v(367, 5) * mm, "end": v(353, 5) * mm});
            skLineSegment(sketch, "E26.12.0.1", {"start": v(366.8, -5) * mm, "end": v(358.49, -5) * mm});
            skArc(sketch, "E26.12.0.2", {"start": v(366.63, 1.4) * mm, "mid": v(366.98, 0.9) * mm, "end": v(367.5, 0.59) * mm});
            skPoint(sketch, "E26.12.0.3", {"position": v(367.5, -5) * mm});
            skPoint(sketch, "E26.12.0.4", {"position": v(352.5, -5) * mm});
            skLineSegment(sketch, "E26.12.0.5", {"start": v(367.5, -4.3) * mm, "end": v(367.5, 0.59) * mm});
            skPoint(sketch, "E26.12.0.6", {"position": v(352.5, 5) * mm});
            skPoint(sketch, "E26.12.0.7", {"position": v(360, 0) * mm});
            skLineSegment(sketch, "E26.12.0.8", {"start": v(352, 2) * mm, "end": v(368, 2) * mm, "construction": true});
            skLineSegment(sketch, "E26.12.0.9", {"start": v(357.51, -5) * mm, "end": v(353.2, -5) * mm});
            skLineSegment(sketch, "E26.12.0.10", {"start": v(352.5, -4.3) * mm, "end": v(352.5, 0.59) * mm});
            skArc(sketch, "E26.12.0.11", {"start": v(352.5, 0.59) * mm, "mid": v(353.02, 0.9) * mm, "end": v(353.37, 1.4) * mm});
            skPoint(sketch, "E26.12.0.12", {"position": v(367.5, 5) * mm});
            skPoint(sketch, "E26.12.0.13", {"position": v(360, 0) * mm});
            skArc(sketch, "E26.12.0.14", {"start": v(366.63, 1.4) * mm, "mid": v(366.98, 0.9) * mm, "end": v(367.5, 0.59) * mm});
            skLineSegment(sketch, "E26.12.0.15", {"start": v(352.5, 3.41) * mm, "end": v(352.5, 4.5) * mm});
            skLineSegment(sketch, "E26.12.0.16", {"start": v(365.7, 2.6) * mm, "end": v(365.7, 1.4) * mm});
            skLineSegment(sketch, "E26.12.0.17", {"start": v(367.5, 4.5) * mm, "end": v(367, 5) * mm});
            skLineSegment(sketch, "E26.12.0.18", {"start": v(367.5, 3.41) * mm, "end": v(367.5, 4.5) * mm});
            skArc(sketch, "E26.12.0.19", {"start": v(353.37, 2.6) * mm, "mid": v(353.02, 3.1) * mm, "end": v(352.5, 3.41) * mm});
            skLineSegment(sketch, "E26.12.0.20", {"start": v(352.5, 4.5) * mm, "end": v(353, 5) * mm});
            skLineSegment(sketch, "E26.12.0.21", {"start": v(352.5, -4.3) * mm, "end": v(353.2, -5) * mm});
            skLineSegment(sketch, "E26.12.0.22", {"start": v(354.3, 2.6) * mm, "end": v(353.37, 2.6) * mm});
            skLineSegment(sketch, "E26.12.0.23", {"start": v(367.5, -4.3) * mm, "end": v(366.8, -5) * mm});
            skLineSegment(sketch, "E26.12.0.24", {"start": v(354.3, 2.6) * mm, "end": v(354.3, 1.4) * mm});
            skArc(sketch, "E26.12.0.25", {"start": v(367.5, 3.41) * mm, "mid": v(366.98, 3.1) * mm, "end": v(366.63, 2.6) * mm});
            skLineSegment(sketch, "E26.12.0.26", {"start": v(365.7, 2.6) * mm, "end": v(366.63, 2.6) * mm});
            skLineSegment(sketch, "E26.12.0.27", {"start": v(365.7, 1.4) * mm, "end": v(366.63, 1.4) * mm});
            skLineSegment(sketch, "E26.12.0.28", {"start": v(354.3, 1.4) * mm, "end": v(353.37, 1.4) * mm});
            skArc(sketch, "E26.12.0.29", {"start": v(358.49, -5) * mm, "mid": v(358, -4.7) * mm, "end": v(357.51, -5) * mm});
            skLineSegment(sketch, "E26.12.0.30", {"start": v(357.51, -5) * mm, "end": v(358.49, -5) * mm, "construction": true});
            skLineSegment(sketch, "E26.13.0.0", {"start": v(397, 5) * mm, "end": v(383, 5) * mm});
            skLineSegment(sketch, "E26.13.0.1", {"start": v(396.8, -5) * mm, "end": v(388.49, -5) * mm});
            skArc(sketch, "E26.13.0.2", {"start": v(396.63, 1.4) * mm, "mid": v(396.98, 0.9) * mm, "end": v(397.5, 0.59) * mm});
            skPoint(sketch, "E26.13.0.3", {"position": v(397.5, -5) * mm});
            skPoint(sketch, "E26.13.0.4", {"position": v(382.5, -5) * mm});
            skLineSegment(sketch, "E26.13.0.5", {"start": v(397.5, -4.3) * mm, "end": v(397.5, 0.59) * mm});
            skPoint(sketch, "E26.13.0.6", {"position": v(382.5, 5) * mm});
            skPoint(sketch, "E26.13.0.7", {"position": v(390, 0) * mm});
            skLineSegment(sketch, "E26.13.0.8", {"start": v(382, 2) * mm, "end": v(398, 2) * mm, "construction": true});
            skLineSegment(sketch, "E26.13.0.9", {"start": v(387.51, -5) * mm, "end": v(383.2, -5) * mm});
            skLineSegment(sketch, "E26.13.0.10", {"start": v(382.5, -4.3) * mm, "end": v(382.5, 0.59) * mm});
            skArc(sketch, "E26.13.0.11", {"start": v(382.5, 0.59) * mm, "mid": v(383.02, 0.9) * mm, "end": v(383.37, 1.4) * mm});
            skPoint(sketch, "E26.13.0.12", {"position": v(397.5, 5) * mm});
            skPoint(sketch, "E26.13.0.13", {"position": v(390, 0) * mm});
            skArc(sketch, "E26.13.0.14", {"start": v(396.63, 1.4) * mm, "mid": v(396.98, 0.9) * mm, "end": v(397.5, 0.59) * mm});
            skLineSegment(sketch, "E26.13.0.15", {"start": v(382.5, 3.41) * mm, "end": v(382.5, 4.5) * mm});
            skLineSegment(sketch, "E26.13.0.16", {"start": v(395.7, 2.6) * mm, "end": v(395.7, 1.4) * mm});
            skLineSegment(sketch, "E26.13.0.17", {"start": v(397.5, 4.5) * mm, "end": v(397, 5) * mm});
            skLineSegment(sketch, "E26.13.0.18", {"start": v(397.5, 3.41) * mm, "end": v(397.5, 4.5) * mm});
            skArc(sketch, "E26.13.0.19", {"start": v(383.37, 2.6) * mm, "mid": v(383.02, 3.1) * mm, "end": v(382.5, 3.41) * mm});
            skLineSegment(sketch, "E26.13.0.20", {"start": v(382.5, 4.5) * mm, "end": v(383, 5) * mm});
            skLineSegment(sketch, "E26.13.0.21", {"start": v(382.5, -4.3) * mm, "end": v(383.2, -5) * mm});
            skLineSegment(sketch, "E26.13.0.22", {"start": v(384.3, 2.6) * mm, "end": v(383.37, 2.6) * mm});
            skLineSegment(sketch, "E26.13.0.23", {"start": v(397.5, -4.3) * mm, "end": v(396.8, -5) * mm});
            skLineSegment(sketch, "E26.13.0.24", {"start": v(384.3, 2.6) * mm, "end": v(384.3, 1.4) * mm});
            skArc(sketch, "E26.13.0.25", {"start": v(397.5, 3.41) * mm, "mid": v(396.98, 3.1) * mm, "end": v(396.63, 2.6) * mm});
            skLineSegment(sketch, "E26.13.0.26", {"start": v(395.7, 2.6) * mm, "end": v(396.63, 2.6) * mm});
            skLineSegment(sketch, "E26.13.0.27", {"start": v(395.7, 1.4) * mm, "end": v(396.63, 1.4) * mm});
            skLineSegment(sketch, "E26.13.0.28", {"start": v(384.3, 1.4) * mm, "end": v(383.37, 1.4) * mm});
            skArc(sketch, "E26.13.0.29", {"start": v(388.49, -5) * mm, "mid": v(388, -4.7) * mm, "end": v(387.51, -5) * mm});
            skLineSegment(sketch, "E26.13.0.30", {"start": v(387.51, -5) * mm, "end": v(388.49, -5) * mm, "construction": true});
            skLineSegment(sketch, "E26.14.0.0", {"start": v(427, 5) * mm, "end": v(413, 5) * mm});
            skLineSegment(sketch, "E26.14.0.1", {"start": v(426.8, -5) * mm, "end": v(418.49, -5) * mm});
            skArc(sketch, "E26.14.0.2", {"start": v(426.63, 1.4) * mm, "mid": v(426.98, 0.9) * mm, "end": v(427.5, 0.59) * mm});
            skPoint(sketch, "E26.14.0.3", {"position": v(427.5, -5) * mm});
            skPoint(sketch, "E26.14.0.4", {"position": v(412.5, -5) * mm});
            skLineSegment(sketch, "E26.14.0.5", {"start": v(427.5, -4.3) * mm, "end": v(427.5, 0.59) * mm});
            skPoint(sketch, "E26.14.0.6", {"position": v(412.5, 5) * mm});
            skPoint(sketch, "E26.14.0.7", {"position": v(420, 0) * mm});
            skLineSegment(sketch, "E26.14.0.8", {"start": v(412, 2) * mm, "end": v(428, 2) * mm, "construction": true});
            skLineSegment(sketch, "E26.14.0.9", {"start": v(417.51, -5) * mm, "end": v(413.2, -5) * mm});
            skLineSegment(sketch, "E26.14.0.10", {"start": v(412.5, -4.3) * mm, "end": v(412.5, 0.59) * mm});
            skArc(sketch, "E26.14.0.11", {"start": v(412.5, 0.59) * mm, "mid": v(413.02, 0.9) * mm, "end": v(413.37, 1.4) * mm});
            skPoint(sketch, "E26.14.0.12", {"position": v(427.5, 5) * mm});
            skPoint(sketch, "E26.14.0.13", {"position": v(420, 0) * mm});
            skArc(sketch, "E26.14.0.14", {"start": v(426.63, 1.4) * mm, "mid": v(426.98, 0.9) * mm, "end": v(427.5, 0.59) * mm});
            skLineSegment(sketch, "E26.14.0.15", {"start": v(412.5, 3.41) * mm, "end": v(412.5, 4.5) * mm});
            skLineSegment(sketch, "E26.14.0.16", {"start": v(425.7, 2.6) * mm, "end": v(425.7, 1.4) * mm});
            skLineSegment(sketch, "E26.14.0.17", {"start": v(427.5, 4.5) * mm, "end": v(427, 5) * mm});
            skLineSegment(sketch, "E26.14.0.18", {"start": v(427.5, 3.41) * mm, "end": v(427.5, 4.5) * mm});
            skArc(sketch, "E26.14.0.19", {"start": v(413.37, 2.6) * mm, "mid": v(413.02, 3.1) * mm, "end": v(412.5, 3.41) * mm});
            skLineSegment(sketch, "E26.14.0.20", {"start": v(412.5, 4.5) * mm, "end": v(413, 5) * mm});
            skLineSegment(sketch, "E26.14.0.21", {"start": v(412.5, -4.3) * mm, "end": v(413.2, -5) * mm});
            skLineSegment(sketch, "E26.14.0.22", {"start": v(414.3, 2.6) * mm, "end": v(413.37, 2.6) * mm});
            skLineSegment(sketch, "E26.14.0.23", {"start": v(427.5, -4.3) * mm, "end": v(426.8, -5) * mm});
            skLineSegment(sketch, "E26.14.0.24", {"start": v(414.3, 2.6) * mm, "end": v(414.3, 1.4) * mm});
            skArc(sketch, "E26.14.0.25", {"start": v(427.5, 3.41) * mm, "mid": v(426.98, 3.1) * mm, "end": v(426.63, 2.6) * mm});
            skLineSegment(sketch, "E26.14.0.26", {"start": v(425.7, 2.6) * mm, "end": v(426.63, 2.6) * mm});
            skLineSegment(sketch, "E26.14.0.27", {"start": v(425.7, 1.4) * mm, "end": v(426.63, 1.4) * mm});
            skLineSegment(sketch, "E26.14.0.28", {"start": v(414.3, 1.4) * mm, "end": v(413.37, 1.4) * mm});
            skArc(sketch, "E26.14.0.29", {"start": v(418.49, -5) * mm, "mid": v(418, -4.7) * mm, "end": v(417.51, -5) * mm});
            skLineSegment(sketch, "E26.14.0.30", {"start": v(417.51, -5) * mm, "end": v(418.49, -5) * mm, "construction": true});
            skLineSegment(sketch, "E26.direction1", {"start": v(-7.5, -5) * mm, "end": v(22.5, -5) * mm, "construction": true});
            skSolve(sketch);
        }
        {
            var Q0;
            Q0=makeQuery(id+"F0.imprint","IMPRINT",FACE,{"disambiguationData":[TD([[makeQuery(id+"F0.imprint","IMPRINT",EDGE,{"derivedFrom":sQuery(id+"F0.wireOp",EDGE,"E1.bottom")}),-1.0]])]});
            extrude(context, id + "F1", {"entities" : qUnion([Q0]), "depth" : 70 * mm, "offsetDistance" : 25 * mm});
        }
        {
            var Q0;
            Q0=makeQuery(id+"F0.imprint","IMPRINT",FACE,{"disambiguationData":[TD([[makeQuery(id+"F0.imprint","IMPRINT",EDGE,{"derivedFrom":sQuery(id+"F0.wireOp",EDGE,"E26.1.0.0")}),1.0]])]});
            extrude(context, id + "F2", {"entities" : qUnion([Q0]), "depth" : 110 * mm, "offsetDistance" : 25 * mm});
        }
        {
            var Q0;
            Q0=makeQuery(id+"F0.imprint","IMPRINT",FACE,{"disambiguationData":[TD([[makeQuery(id+"F0.imprint","IMPRINT",EDGE,{"derivedFrom":sQuery(id+"F0.wireOp",EDGE,"E26.2.0.0")}),1.0]])]});
            extrude(context, id + "F3", {"entities" : qUnion([Q0]), "depth" : 150 * mm, "offsetDistance" : 25 * mm});
        }
        {
            var Q0;
            Q0=makeQuery(id+"F0.imprint","IMPRINT",FACE,{"disambiguationData":[TD([[makeQuery(id+"F0.imprint","IMPRINT",EDGE,{"derivedFrom":sQuery(id+"F0.wireOp",EDGE,"E26.3.0.0")}),1.0]])]});
            extrude(context, id + "F4", {"entities" : qUnion([Q0]), "depth" : 190 * mm, "offsetDistance" : 25 * mm});
        }
        {
            var Q0;
            Q0=makeQuery(id+"F0.imprint","IMPRINT",FACE,{"disambiguationData":[TD([[makeQuery(id+"F0.imprint","IMPRINT",EDGE,{"derivedFrom":sQuery(id+"F0.wireOp",EDGE,"E26.4.0.0")}),1.0]])]});
            extrude(context, id + "F5", {"entities" : qUnion([Q0]), "depth" : 230 * mm, "offsetDistance" : 25 * mm});
        }
        {
            var Q0;
            Q0=makeQuery(id+"F0.imprint","IMPRINT",FACE,{"disambiguationData":[TD([[makeQuery(id+"F0.imprint","IMPRINT",EDGE,{"derivedFrom":sQuery(id+"F0.wireOp",EDGE,"E26.5.0.0")}),1.0]])]});
            extrude(context, id + "F6", {"entities" : qUnion([Q0]), "depth" : 270 * mm, "offsetDistance" : 25 * mm});
        }
        {
            var Q0;
            Q0=makeQuery(id+"F0.imprint","IMPRINT",FACE,{"disambiguationData":[TD([[makeQuery(id+"F0.imprint","IMPRINT",EDGE,{"derivedFrom":sQuery(id+"F0.wireOp",EDGE,"E26.6.0.0")}),1.0]])]});
            extrude(context, id + "F7", {"entities" : qUnion([Q0]), "depth" : 310 * mm, "offsetDistance" : 25 * mm});
        }
        {
            var Q0;
            Q0=makeQuery(id+"F0.imprint","IMPRINT",FACE,{"disambiguationData":[TD([[makeQuery(id+"F0.imprint","IMPRINT",EDGE,{"derivedFrom":sQuery(id+"F0.wireOp",EDGE,"E26.7.0.0")}),1.0]])]});
            extrude(context, id + "F8", {"entities" : qUnion([Q0]), "depth" : 350 * mm, "offsetDistance" : 25 * mm});
        }
        {
            var Q0;
            Q0=makeQuery(id+"F0.imprint","IMPRINT",FACE,{"disambiguationData":[TD([[makeQuery(id+"F0.imprint","IMPRINT",EDGE,{"derivedFrom":sQuery(id+"F0.wireOp",EDGE,"E26.8.0.0")}),1.0]])]});
            extrude(context, id + "F9", {"entities" : qUnion([Q0]), "depth" : 390 * mm, "offsetDistance" : 25 * mm});
        }
        {
            var Q0;
            Q0=makeQuery(id+"F0.imprint","IMPRINT",FACE,{"disambiguationData":[TD([[makeQuery(id+"F0.imprint","IMPRINT",EDGE,{"derivedFrom":sQuery(id+"F0.wireOp",EDGE,"E26.9.0.0")}),1.0]])]});
            extrude(context, id + "F10", {"entities" : qUnion([Q0]), "depth" : 430 * mm, "offsetDistance" : 25 * mm});
        }
        {
            var Q0;
            Q0=makeQuery(id+"F0.imprint","IMPRINT",FACE,{"disambiguationData":[TD([[makeQuery(id+"F0.imprint","IMPRINT",EDGE,{"derivedFrom":sQuery(id+"F0.wireOp",EDGE,"E26.10.0.0")}),1.0]])]});
            extrude(context, id + "F11", {"entities" : qUnion([Q0]), "depth" : 470 * mm, "offsetDistance" : 25 * mm});
        }
        {
            var Q0;
            Q0=makeQuery(id+"F0.imprint","IMPRINT",FACE,{"disambiguationData":[TD([[makeQuery(id+"F0.imprint","IMPRINT",EDGE,{"derivedFrom":sQuery(id+"F0.wireOp",EDGE,"E26.11.0.0")}),1.0]])]});
            extrude(context, id + "F12", {"entities" : qUnion([Q0]), "depth" : 550 * mm, "offsetDistance" : 25 * mm});
        }
        {
            var Q0;
            Q0=makeQuery(id+"F0.imprint","IMPRINT",FACE,{"disambiguationData":[TD([[makeQuery(id+"F0.imprint","IMPRINT",EDGE,{"derivedFrom":sQuery(id+"F0.wireOp",EDGE,"E26.12.0.0")}),1.0]])]});
            extrude(context, id + "F13", {"entities" : qUnion([Q0]), "depth" : 670 * mm, "offsetDistance" : 25 * mm});
        }
        {
            var Q0;
            Q0=makeQuery(id+"F0.imprint","IMPRINT",FACE,{"disambiguationData":[TD([[makeQuery(id+"F0.imprint","IMPRINT",EDGE,{"derivedFrom":sQuery(id+"F0.wireOp",EDGE,"E26.13.0.0")}),1.0]])]});
            extrude(context, id + "F14", {"entities" : qUnion([Q0]), "depth" : 870 * mm, "offsetDistance" : 25 * mm});
        }
        {
            var Q0;
            Q0=makeQuery(id+"F0.imprint","IMPRINT",FACE,{"disambiguationData":[TD([[makeQuery(id+"F0.imprint","IMPRINT",EDGE,{"derivedFrom":sQuery(id+"F0.wireOp",EDGE,"E26.14.0.0")}),1.0]])]});
            extrude(context, id + "F15", {"entities" : qUnion([Q0]), "depth" : 1990 * mm, "offsetDistance" : 25 * mm});
        }
        {
            var Q0;
            Q0=makeQuery(id+"F1.opExtrude","SWEPT_FACE",FACE,{"disambiguationData":[OSD([sQuery(id+"F0.wireOp",EDGE,"E1.top")])]});
            var sketch = newSketch(context, id + "F16", { "sketchPlane" : qUnion([Q0])});
            skPoint(sketch, "E27", {"position": v(0, -15) * mm});
            skPoint(sketch, "E28.1.0.0", {"position": v(30, -15) * mm});
            skPoint(sketch, "E28.2.0.0", {"position": v(60, -15) * mm});
            skPoint(sketch, "E28.3.0.0", {"position": v(90, -15) * mm});
            skPoint(sketch, "E28.4.0.0", {"position": v(120, -15) * mm});
            skPoint(sketch, "E28.5.0.0", {"position": v(150, -15) * mm});
            skPoint(sketch, "E28.6.0.0", {"position": v(180, -15) * mm});
            skLineSegment(sketch, "E28.direction1", {"start": v(0, -15) * mm, "end": v(30, -15) * mm, "construction": true});
            skPoint(sketch, "E29.1.0.0", {"position": v(0, -55) * mm});
            skPoint(sketch, "E29.1.0.1", {"position": v(30, -55) * mm});
            skPoint(sketch, "E29.1.0.2", {"position": v(60, -55) * mm});
            skPoint(sketch, "E29.1.0.3", {"position": v(90, -55) * mm});
            skPoint(sketch, "E29.1.0.4", {"position": v(120, -55) * mm});
            skPoint(sketch, "E29.1.0.5", {"position": v(150, -55) * mm});
            skPoint(sketch, "E29.1.0.6", {"position": v(180, -55) * mm});
            skPoint(sketch, "E29.2.0.0", {"position": v(0, -95) * mm});
            skPoint(sketch, "E29.2.0.1", {"position": v(30, -95) * mm});
            skPoint(sketch, "E29.2.0.2", {"position": v(60, -95) * mm});
            skPoint(sketch, "E29.2.0.3", {"position": v(90, -95) * mm});
            skPoint(sketch, "E29.2.0.4", {"position": v(120, -95) * mm});
            skPoint(sketch, "E29.2.0.5", {"position": v(150, -95) * mm});
            skPoint(sketch, "E29.2.0.6", {"position": v(180, -95) * mm});
            skPoint(sketch, "E29.3.0.0", {"position": v(0, -135) * mm});
            skPoint(sketch, "E29.3.0.1", {"position": v(30, -135) * mm});
            skPoint(sketch, "E29.3.0.2", {"position": v(60, -135) * mm});
            skPoint(sketch, "E29.3.0.3", {"position": v(90, -135) * mm});
            skPoint(sketch, "E29.3.0.4", {"position": v(120, -135) * mm});
            skPoint(sketch, "E29.3.0.5", {"position": v(150, -135) * mm});
            skPoint(sketch, "E29.3.0.6", {"position": v(180, -135) * mm});
            skPoint(sketch, "E29.4.0.0", {"position": v(0, -175) * mm});
            skPoint(sketch, "E29.4.0.1", {"position": v(30, -175) * mm});
            skPoint(sketch, "E29.4.0.2", {"position": v(60, -175) * mm});
            skPoint(sketch, "E29.4.0.3", {"position": v(90, -175) * mm});
            skPoint(sketch, "E29.4.0.4", {"position": v(120, -175) * mm});
            skPoint(sketch, "E29.4.0.5", {"position": v(150, -175) * mm});
            skPoint(sketch, "E29.4.0.6", {"position": v(180, -175) * mm});
            skPoint(sketch, "E29.5.0.0", {"position": v(0, -215) * mm});
            skPoint(sketch, "E29.5.0.1", {"position": v(30, -215) * mm});
            skPoint(sketch, "E29.5.0.2", {"position": v(60, -215) * mm});
            skPoint(sketch, "E29.5.0.3", {"position": v(90, -215) * mm});
            skPoint(sketch, "E29.5.0.4", {"position": v(120, -215) * mm});
            skPoint(sketch, "E29.5.0.5", {"position": v(150, -215) * mm});
            skPoint(sketch, "E29.5.0.6", {"position": v(180, -215) * mm});
            skPoint(sketch, "E29.6.0.0", {"position": v(0, -255) * mm});
            skPoint(sketch, "E29.6.0.1", {"position": v(30, -255) * mm});
            skPoint(sketch, "E29.6.0.2", {"position": v(60, -255) * mm});
            skPoint(sketch, "E29.6.0.3", {"position": v(90, -255) * mm});
            skPoint(sketch, "E29.6.0.4", {"position": v(120, -255) * mm});
            skPoint(sketch, "E29.6.0.5", {"position": v(150, -255) * mm});
            skPoint(sketch, "E29.6.0.6", {"position": v(180, -255) * mm});
            skPoint(sketch, "E29.7.0.0", {"position": v(0, -295) * mm});
            skPoint(sketch, "E29.7.0.1", {"position": v(30, -295) * mm});
            skPoint(sketch, "E29.7.0.2", {"position": v(60, -295) * mm});
            skPoint(sketch, "E29.7.0.3", {"position": v(90, -295) * mm});
            skPoint(sketch, "E29.7.0.4", {"position": v(120, -295) * mm});
            skPoint(sketch, "E29.7.0.5", {"position": v(150, -295) * mm});
            skPoint(sketch, "E29.7.0.6", {"position": v(180, -295) * mm});
            skLineSegment(sketch, "E29.direction1", {"start": v(0, -15) * mm, "end": v(0, -55) * mm, "construction": true});
            skPoint(sketch, "E30.0.7.0", {"position": v(210, -15) * mm});
            skPoint(sketch, "E30.0.8.0", {"position": v(240, -15) * mm});
            skPoint(sketch, "E30.0.9.0", {"position": v(270, -15) * mm});
            skPoint(sketch, "E30.0.10.0", {"position": v(300, -15) * mm});
            skPoint(sketch, "E31.1.0.0", {"position": v(300, -55) * mm});
            skPoint(sketch, "E31.1.0.1", {"position": v(270, -55) * mm});
            skPoint(sketch, "E31.1.0.2", {"position": v(240, -55) * mm});
            skPoint(sketch, "E31.1.0.3", {"position": v(210, -55) * mm});
            skPoint(sketch, "E31.2.0.0", {"position": v(300, -95) * mm});
            skPoint(sketch, "E31.2.0.1", {"position": v(270, -95) * mm});
            skPoint(sketch, "E31.2.0.2", {"position": v(240, -95) * mm});
            skPoint(sketch, "E31.2.0.3", {"position": v(210, -95) * mm});
            skLineSegment(sketch, "E31.direction1", {"start": v(210, -15) * mm, "end": v(210, -55) * mm, "construction": true});
            skPoint(sketch, "E32.0.3.0", {"position": v(300, -135) * mm});
            skPoint(sketch, "E32.1.3.0", {"position": v(270, -135) * mm});
            skPoint(sketch, "E32.2.3.0", {"position": v(240, -135) * mm});
            skPoint(sketch, "E32.3.3.0", {"position": v(210, -135) * mm});
            skPoint(sketch, "E32.0.4.0", {"position": v(300, -175) * mm});
            skPoint(sketch, "E32.1.4.0", {"position": v(270, -175) * mm});
            skPoint(sketch, "E32.2.4.0", {"position": v(240, -175) * mm});
            skPoint(sketch, "E32.3.4.0", {"position": v(210, -175) * mm});
            skPoint(sketch, "E32.0.5.0", {"position": v(300, -215) * mm});
            skPoint(sketch, "E32.1.5.0", {"position": v(270, -215) * mm});
            skPoint(sketch, "E32.2.5.0", {"position": v(240, -215) * mm});
            skPoint(sketch, "E32.3.5.0", {"position": v(210, -215) * mm});
            skPoint(sketch, "E32.0.6.0", {"position": v(300, -255) * mm});
            skPoint(sketch, "E32.1.6.0", {"position": v(270, -255) * mm});
            skPoint(sketch, "E32.2.6.0", {"position": v(240, -255) * mm});
            skPoint(sketch, "E32.3.6.0", {"position": v(210, -255) * mm});
            skPoint(sketch, "E32.0.7.0", {"position": v(300, -295) * mm});
            skPoint(sketch, "E32.1.7.0", {"position": v(270, -295) * mm});
            skPoint(sketch, "E32.2.7.0", {"position": v(240, -295) * mm});
            skPoint(sketch, "E32.3.7.0", {"position": v(210, -295) * mm});
            skPoint(sketch, "E32.0.8.0", {"position": v(300, -335) * mm});
            skPoint(sketch, "E32.1.8.0", {"position": v(270, -335) * mm});
            skPoint(sketch, "E32.2.8.0", {"position": v(240, -335) * mm});
            skPoint(sketch, "E32.3.8.0", {"position": v(210, -335) * mm});
            skPoint(sketch, "E32.0.9.0", {"position": v(300, -375) * mm});
            skPoint(sketch, "E32.1.9.0", {"position": v(270, -375) * mm});
            skPoint(sketch, "E32.2.9.0", {"position": v(240, -375) * mm});
            skPoint(sketch, "E32.3.9.0", {"position": v(210, -375) * mm});
            skPoint(sketch, "E32.0.10.0", {"position": v(300, -415) * mm});
            skPoint(sketch, "E32.1.10.0", {"position": v(270, -415) * mm});
            skPoint(sketch, "E32.2.10.0", {"position": v(240, -415) * mm});
            skPoint(sketch, "E32.3.10.0", {"position": v(210, -415) * mm});
            skPoint(sketch, "E32.0.11.0", {"position": v(300, -455) * mm});
            skPoint(sketch, "E32.1.11.0", {"position": v(270, -455) * mm});
            skPoint(sketch, "E32.2.11.0", {"position": v(240, -455) * mm});
            skPoint(sketch, "E32.3.11.0", {"position": v(210, -455) * mm});
            skPoint(sketch, "E33.0.11.0", {"position": v(330, -15) * mm});
            skPoint(sketch, "E33.0.12.0", {"position": v(360, -15) * mm});
            skPoint(sketch, "E33.0.13.0", {"position": v(390, -15) * mm});
            skPoint(sketch, "E33.0.14.0", {"position": v(420, -15) * mm});
            skPoint(sketch, "E34.1.0.0", {"position": v(420, -55) * mm});
            skPoint(sketch, "E34.1.0.1", {"position": v(330, -55) * mm});
            skPoint(sketch, "E34.1.0.2", {"position": v(390, -55) * mm});
            skPoint(sketch, "E34.1.0.3", {"position": v(360, -55) * mm});
            skPoint(sketch, "E34.2.0.0", {"position": v(420, -95) * mm});
            skPoint(sketch, "E34.2.0.1", {"position": v(330, -95) * mm});
            skPoint(sketch, "E34.2.0.2", {"position": v(390, -95) * mm});
            skPoint(sketch, "E34.2.0.3", {"position": v(360, -95) * mm});
            skLineSegment(sketch, "E34.direction1", {"start": v(330, -15) * mm, "end": v(330, -55) * mm, "construction": true});
            skPoint(sketch, "E35.0.3.0", {"position": v(420, -135) * mm});
            skPoint(sketch, "E35.1.3.0", {"position": v(330, -135) * mm});
            skPoint(sketch, "E35.2.3.0", {"position": v(390, -135) * mm});
            skPoint(sketch, "E35.3.3.0", {"position": v(360, -135) * mm});
            skPoint(sketch, "E35.0.4.0", {"position": v(420, -175) * mm});
            skPoint(sketch, "E35.1.4.0", {"position": v(330, -175) * mm});
            skPoint(sketch, "E35.2.4.0", {"position": v(390, -175) * mm});
            skPoint(sketch, "E35.3.4.0", {"position": v(360, -175) * mm});
            skPoint(sketch, "E35.0.5.0", {"position": v(420, -215) * mm});
            skPoint(sketch, "E35.1.5.0", {"position": v(330, -215) * mm});
            skPoint(sketch, "E35.2.5.0", {"position": v(390, -215) * mm});
            skPoint(sketch, "E35.3.5.0", {"position": v(360, -215) * mm});
            skPoint(sketch, "E35.0.6.0", {"position": v(420, -255) * mm});
            skPoint(sketch, "E35.1.6.0", {"position": v(330, -255) * mm});
            skPoint(sketch, "E35.2.6.0", {"position": v(390, -255) * mm});
            skPoint(sketch, "E35.3.6.0", {"position": v(360, -255) * mm});
            skPoint(sketch, "E35.0.7.0", {"position": v(420, -295) * mm});
            skPoint(sketch, "E35.1.7.0", {"position": v(330, -295) * mm});
            skPoint(sketch, "E35.2.7.0", {"position": v(390, -295) * mm});
            skPoint(sketch, "E35.3.7.0", {"position": v(360, -295) * mm});
            skPoint(sketch, "E35.0.8.0", {"position": v(420, -335) * mm});
            skPoint(sketch, "E35.1.8.0", {"position": v(330, -335) * mm});
            skPoint(sketch, "E35.2.8.0", {"position": v(390, -335) * mm});
            skPoint(sketch, "E35.3.8.0", {"position": v(360, -335) * mm});
            skPoint(sketch, "E35.0.9.0", {"position": v(420, -375) * mm});
            skPoint(sketch, "E35.1.9.0", {"position": v(330, -375) * mm});
            skPoint(sketch, "E35.2.9.0", {"position": v(390, -375) * mm});
            skPoint(sketch, "E35.3.9.0", {"position": v(360, -375) * mm});
            skPoint(sketch, "E35.0.10.0", {"position": v(420, -415) * mm});
            skPoint(sketch, "E35.1.10.0", {"position": v(330, -415) * mm});
            skPoint(sketch, "E35.2.10.0", {"position": v(390, -415) * mm});
            skPoint(sketch, "E35.3.10.0", {"position": v(360, -415) * mm});
            skPoint(sketch, "E35.0.11.0", {"position": v(420, -455) * mm});
            skPoint(sketch, "E35.1.11.0", {"position": v(330, -455) * mm});
            skPoint(sketch, "E35.2.11.0", {"position": v(390, -455) * mm});
            skPoint(sketch, "E35.3.11.0", {"position": v(360, -455) * mm});
            skPoint(sketch, "E35.0.12.0", {"position": v(420, -495) * mm});
            skPoint(sketch, "E35.1.12.0", {"position": v(330, -495) * mm});
            skPoint(sketch, "E35.2.12.0", {"position": v(390, -495) * mm});
            skPoint(sketch, "E35.3.12.0", {"position": v(360, -495) * mm});
            skPoint(sketch, "E35.0.13.0", {"position": v(420, -535) * mm});
            skPoint(sketch, "E35.1.13.0", {"position": v(330, -535) * mm});
            skPoint(sketch, "E35.2.13.0", {"position": v(390, -535) * mm});
            skPoint(sketch, "E35.3.13.0", {"position": v(360, -535) * mm});
            skPoint(sketch, "E35.0.14.0", {"position": v(420, -575) * mm});
            skPoint(sketch, "E35.1.14.0", {"position": v(330, -575) * mm});
            skPoint(sketch, "E35.2.14.0", {"position": v(390, -575) * mm});
            skPoint(sketch, "E35.3.14.0", {"position": v(360, -575) * mm});
            skPoint(sketch, "E35.0.15.0", {"position": v(420, -615) * mm});
            skPoint(sketch, "E35.1.15.0", {"position": v(330, -615) * mm});
            skPoint(sketch, "E35.2.15.0", {"position": v(390, -615) * mm});
            skPoint(sketch, "E35.3.15.0", {"position": v(360, -615) * mm});
            skPoint(sketch, "E35.0.16.0", {"position": v(420, -655) * mm});
            skPoint(sketch, "E35.1.16.0", {"position": v(330, -655) * mm});
            skPoint(sketch, "E35.2.16.0", {"position": v(390, -655) * mm});
            skPoint(sketch, "E35.3.16.0", {"position": v(360, -655) * mm});
            skPoint(sketch, "E35.0.17.0", {"position": v(420, -695) * mm});
            skPoint(sketch, "E35.1.17.0", {"position": v(330, -695) * mm});
            skPoint(sketch, "E35.2.17.0", {"position": v(390, -695) * mm});
            skPoint(sketch, "E35.3.17.0", {"position": v(360, -695) * mm});
            skPoint(sketch, "E35.0.18.0", {"position": v(420, -735) * mm});
            skPoint(sketch, "E35.1.18.0", {"position": v(330, -735) * mm});
            skPoint(sketch, "E35.2.18.0", {"position": v(390, -735) * mm});
            skPoint(sketch, "E35.3.18.0", {"position": v(360, -735) * mm});
            skPoint(sketch, "E35.0.19.0", {"position": v(420, -775) * mm});
            skPoint(sketch, "E35.1.19.0", {"position": v(330, -775) * mm});
            skPoint(sketch, "E35.2.19.0", {"position": v(390, -775) * mm});
            skPoint(sketch, "E35.3.19.0", {"position": v(360, -775) * mm});
            skPoint(sketch, "E35.0.20.0", {"position": v(420, -815) * mm});
            skPoint(sketch, "E35.1.20.0", {"position": v(330, -815) * mm});
            skPoint(sketch, "E35.2.20.0", {"position": v(390, -815) * mm});
            skPoint(sketch, "E35.3.20.0", {"position": v(360, -815) * mm});
            skPoint(sketch, "E35.0.21.0", {"position": v(420, -855) * mm});
            skPoint(sketch, "E35.1.21.0", {"position": v(330, -855) * mm});
            skPoint(sketch, "E35.2.21.0", {"position": v(390, -855) * mm});
            skPoint(sketch, "E35.3.21.0", {"position": v(360, -855) * mm});
            skPoint(sketch, "E35.0.22.0", {"position": v(420, -895) * mm});
            skPoint(sketch, "E35.1.22.0", {"position": v(330, -895) * mm});
            skPoint(sketch, "E35.2.22.0", {"position": v(390, -895) * mm});
            skPoint(sketch, "E35.3.22.0", {"position": v(360, -895) * mm});
            skPoint(sketch, "E35.0.23.0", {"position": v(420, -935) * mm});
            skPoint(sketch, "E35.1.23.0", {"position": v(330, -935) * mm});
            skPoint(sketch, "E35.2.23.0", {"position": v(390, -935) * mm});
            skPoint(sketch, "E35.3.23.0", {"position": v(360, -935) * mm});
            skPoint(sketch, "E35.0.24.0", {"position": v(420, -975) * mm});
            skPoint(sketch, "E35.1.24.0", {"position": v(330, -975) * mm});
            skPoint(sketch, "E35.2.24.0", {"position": v(390, -975) * mm});
            skPoint(sketch, "E35.3.24.0", {"position": v(360, -975) * mm});
            skPoint(sketch, "E35.0.25.0", {"position": v(420, -1015) * mm});
            skPoint(sketch, "E35.1.25.0", {"position": v(330, -1015) * mm});
            skPoint(sketch, "E35.2.25.0", {"position": v(390, -1015) * mm});
            skPoint(sketch, "E35.3.25.0", {"position": v(360, -1015) * mm});
            skPoint(sketch, "E35.0.26.0", {"position": v(420, -1055) * mm});
            skPoint(sketch, "E35.1.26.0", {"position": v(330, -1055) * mm});
            skPoint(sketch, "E35.2.26.0", {"position": v(390, -1055) * mm});
            skPoint(sketch, "E35.3.26.0", {"position": v(360, -1055) * mm});
            skPoint(sketch, "E35.0.27.0", {"position": v(420, -1095) * mm});
            skPoint(sketch, "E35.1.27.0", {"position": v(330, -1095) * mm});
            skPoint(sketch, "E35.2.27.0", {"position": v(390, -1095) * mm});
            skPoint(sketch, "E35.3.27.0", {"position": v(360, -1095) * mm});
            skPoint(sketch, "E35.0.28.0", {"position": v(420, -1135) * mm});
            skPoint(sketch, "E35.1.28.0", {"position": v(330, -1135) * mm});
            skPoint(sketch, "E35.2.28.0", {"position": v(390, -1135) * mm});
            skPoint(sketch, "E35.3.28.0", {"position": v(360, -1135) * mm});
            skPoint(sketch, "E35.0.29.0", {"position": v(420, -1175) * mm});
            skPoint(sketch, "E35.1.29.0", {"position": v(330, -1175) * mm});
            skPoint(sketch, "E35.2.29.0", {"position": v(390, -1175) * mm});
            skPoint(sketch, "E35.3.29.0", {"position": v(360, -1175) * mm});
            skPoint(sketch, "E35.0.30.0", {"position": v(420, -1215) * mm});
            skPoint(sketch, "E35.1.30.0", {"position": v(330, -1215) * mm});
            skPoint(sketch, "E35.2.30.0", {"position": v(390, -1215) * mm});
            skPoint(sketch, "E35.3.30.0", {"position": v(360, -1215) * mm});
            skPoint(sketch, "E35.0.31.0", {"position": v(420, -1255) * mm});
            skPoint(sketch, "E35.1.31.0", {"position": v(330, -1255) * mm});
            skPoint(sketch, "E35.2.31.0", {"position": v(390, -1255) * mm});
            skPoint(sketch, "E35.3.31.0", {"position": v(360, -1255) * mm});
            skPoint(sketch, "E35.0.32.0", {"position": v(420, -1295) * mm});
            skPoint(sketch, "E35.1.32.0", {"position": v(330, -1295) * mm});
            skPoint(sketch, "E35.2.32.0", {"position": v(390, -1295) * mm});
            skPoint(sketch, "E35.3.32.0", {"position": v(360, -1295) * mm});
            skPoint(sketch, "E35.0.33.0", {"position": v(420, -1335) * mm});
            skPoint(sketch, "E35.1.33.0", {"position": v(330, -1335) * mm});
            skPoint(sketch, "E35.2.33.0", {"position": v(390, -1335) * mm});
            skPoint(sketch, "E35.3.33.0", {"position": v(360, -1335) * mm});
            skPoint(sketch, "E35.0.34.0", {"position": v(420, -1375) * mm});
            skPoint(sketch, "E35.1.34.0", {"position": v(330, -1375) * mm});
            skPoint(sketch, "E35.2.34.0", {"position": v(390, -1375) * mm});
            skPoint(sketch, "E35.3.34.0", {"position": v(360, -1375) * mm});
            skPoint(sketch, "E35.0.35.0", {"position": v(420, -1415) * mm});
            skPoint(sketch, "E35.1.35.0", {"position": v(330, -1415) * mm});
            skPoint(sketch, "E35.2.35.0", {"position": v(390, -1415) * mm});
            skPoint(sketch, "E35.3.35.0", {"position": v(360, -1415) * mm});
            skPoint(sketch, "E35.0.36.0", {"position": v(420, -1455) * mm});
            skPoint(sketch, "E35.1.36.0", {"position": v(330, -1455) * mm});
            skPoint(sketch, "E35.2.36.0", {"position": v(390, -1455) * mm});
            skPoint(sketch, "E35.3.36.0", {"position": v(360, -1455) * mm});
            skPoint(sketch, "E35.0.37.0", {"position": v(420, -1495) * mm});
            skPoint(sketch, "E35.1.37.0", {"position": v(330, -1495) * mm});
            skPoint(sketch, "E35.2.37.0", {"position": v(390, -1495) * mm});
            skPoint(sketch, "E35.3.37.0", {"position": v(360, -1495) * mm});
            skPoint(sketch, "E35.0.38.0", {"position": v(420, -1535) * mm});
            skPoint(sketch, "E35.1.38.0", {"position": v(330, -1535) * mm});
            skPoint(sketch, "E35.2.38.0", {"position": v(390, -1535) * mm});
            skPoint(sketch, "E35.3.38.0", {"position": v(360, -1535) * mm});
            skPoint(sketch, "E35.0.39.0", {"position": v(420, -1575) * mm});
            skPoint(sketch, "E35.1.39.0", {"position": v(330, -1575) * mm});
            skPoint(sketch, "E35.2.39.0", {"position": v(390, -1575) * mm});
            skPoint(sketch, "E35.3.39.0", {"position": v(360, -1575) * mm});
            skPoint(sketch, "E35.0.40.0", {"position": v(420, -1615) * mm});
            skPoint(sketch, "E35.1.40.0", {"position": v(330, -1615) * mm});
            skPoint(sketch, "E35.2.40.0", {"position": v(390, -1615) * mm});
            skPoint(sketch, "E35.3.40.0", {"position": v(360, -1615) * mm});
            skPoint(sketch, "E35.0.41.0", {"position": v(420, -1655) * mm});
            skPoint(sketch, "E35.1.41.0", {"position": v(330, -1655) * mm});
            skPoint(sketch, "E35.2.41.0", {"position": v(390, -1655) * mm});
            skPoint(sketch, "E35.3.41.0", {"position": v(360, -1655) * mm});
            skPoint(sketch, "E35.0.42.0", {"position": v(420, -1695) * mm});
            skPoint(sketch, "E35.1.42.0", {"position": v(330, -1695) * mm});
            skPoint(sketch, "E35.2.42.0", {"position": v(390, -1695) * mm});
            skPoint(sketch, "E35.3.42.0", {"position": v(360, -1695) * mm});
            skPoint(sketch, "E35.0.43.0", {"position": v(420, -1735) * mm});
            skPoint(sketch, "E35.1.43.0", {"position": v(330, -1735) * mm});
            skPoint(sketch, "E35.2.43.0", {"position": v(390, -1735) * mm});
            skPoint(sketch, "E35.3.43.0", {"position": v(360, -1735) * mm});
            skPoint(sketch, "E35.0.44.0", {"position": v(420, -1775) * mm});
            skPoint(sketch, "E35.1.44.0", {"position": v(330, -1775) * mm});
            skPoint(sketch, "E35.2.44.0", {"position": v(390, -1775) * mm});
            skPoint(sketch, "E35.3.44.0", {"position": v(360, -1775) * mm});
            skPoint(sketch, "E35.0.45.0", {"position": v(420, -1815) * mm});
            skPoint(sketch, "E35.1.45.0", {"position": v(330, -1815) * mm});
            skPoint(sketch, "E35.2.45.0", {"position": v(390, -1815) * mm});
            skPoint(sketch, "E35.3.45.0", {"position": v(360, -1815) * mm});
            skPoint(sketch, "E35.0.46.0", {"position": v(420, -1855) * mm});
            skPoint(sketch, "E35.1.46.0", {"position": v(330, -1855) * mm});
            skPoint(sketch, "E35.2.46.0", {"position": v(390, -1855) * mm});
            skPoint(sketch, "E35.3.46.0", {"position": v(360, -1855) * mm});
            skPoint(sketch, "E35.0.47.0", {"position": v(420, -1895) * mm});
            skPoint(sketch, "E35.1.47.0", {"position": v(330, -1895) * mm});
            skPoint(sketch, "E35.2.47.0", {"position": v(390, -1895) * mm});
            skPoint(sketch, "E35.3.47.0", {"position": v(360, -1895) * mm});
            skPoint(sketch, "E35.0.48.0", {"position": v(420, -1935) * mm});
            skPoint(sketch, "E35.1.48.0", {"position": v(330, -1935) * mm});
            skPoint(sketch, "E35.2.48.0", {"position": v(390, -1935) * mm});
            skPoint(sketch, "E35.3.48.0", {"position": v(360, -1935) * mm});
            skPoint(sketch, "E35.0.49.0", {"position": v(420, -1975) * mm});
            skPoint(sketch, "E35.1.49.0", {"position": v(330, -1975) * mm});
            skPoint(sketch, "E35.2.49.0", {"position": v(390, -1975) * mm});
            skPoint(sketch, "E35.3.49.0", {"position": v(360, -1975) * mm});
            skSolve(sketch);
        }
        {
            var Q0;
            Q0=sQuery(id+"F16.wireOp",VERTEX,"E30.0.10.0");
            var Q1;
            Q1=sQuery(id+"F16.wireOp",VERTEX,"E32.0.9.0");
            var Q2;
            Q2=sQuery(id+"F16.wireOp",VERTEX,"E32.0.4.0");
            var Q3;
            Q3=sQuery(id+"F16.wireOp",VERTEX,"E32.0.5.0");
            var Q4;
            Q4=sQuery(id+"F16.wireOp",VERTEX,"E32.0.8.0");
            var Q5;
            Q5=sQuery(id+"F16.wireOp",VERTEX,"E31.1.0.0");
            var Q6;
            Q6=sQuery(id+"F16.wireOp",VERTEX,"E31.2.0.0");
            var Q7;
            Q7=sQuery(id+"F16.wireOp",VERTEX,"E32.0.6.0");
            var Q8;
            Q8=sQuery(id+"F16.wireOp",VERTEX,"E32.0.11.0");
            var Q9;
            Q9=sQuery(id+"F16.wireOp",VERTEX,"E32.0.7.0");
            var Q10;
            Q10=sQuery(id+"F16.wireOp",VERTEX,"E32.0.10.0");
            var Q11;
            Q11=sQuery(id+"F16.wireOp",VERTEX,"E32.0.3.0");
            var Q12;
            Q12=sQuery(id+"F16.wireOp",VERTEX,"E31.2.0.1");
            var Q13;
            Q13=sQuery(id+"F16.wireOp",VERTEX,"E30.0.9.0");
            var Q14;
            Q14=sQuery(id+"F16.wireOp",VERTEX,"E32.1.5.0");
            var Q15;
            Q15=sQuery(id+"F16.wireOp",VERTEX,"E31.1.0.1");
            var Q16;
            Q16=sQuery(id+"F16.wireOp",VERTEX,"E32.1.9.0");
            var Q17;
            Q17=sQuery(id+"F16.wireOp",VERTEX,"E32.1.10.0");
            var Q18;
            Q18=sQuery(id+"F16.wireOp",VERTEX,"E32.1.7.0");
            var Q19;
            Q19=sQuery(id+"F16.wireOp",VERTEX,"E32.1.4.0");
            var Q20;
            Q20=sQuery(id+"F16.wireOp",VERTEX,"E32.1.3.0");
            var Q21;
            Q21=sQuery(id+"F16.wireOp",VERTEX,"E32.1.8.0");
            var Q22;
            Q22=sQuery(id+"F16.wireOp",VERTEX,"E32.1.6.0");
            var Q23;
            Q23=sQuery(id+"F16.wireOp",VERTEX,"E31.2.0.2");
            var Q24;
            Q24=sQuery(id+"F16.wireOp",VERTEX,"E31.1.0.2");
            var Q25;
            Q25=sQuery(id+"F16.wireOp",VERTEX,"E32.2.8.0");
            var Q26;
            Q26=sQuery(id+"F16.wireOp",VERTEX,"E32.2.5.0");
            var Q27;
            Q27=sQuery(id+"F16.wireOp",VERTEX,"E32.2.4.0");
            var Q28;
            Q28=sQuery(id+"F16.wireOp",VERTEX,"E32.2.9.0");
            var Q29;
            Q29=sQuery(id+"F16.wireOp",VERTEX,"E32.2.7.0");
            var Q30;
            Q30=sQuery(id+"F16.wireOp",VERTEX,"E30.0.8.0");
            var Q31;
            Q31=sQuery(id+"F16.wireOp",VERTEX,"E32.2.3.0");
            var Q32;
            Q32=sQuery(id+"F16.wireOp",VERTEX,"E32.2.6.0");
            var Q33;
            Q33=sQuery(id+"F16.wireOp",VERTEX,"E32.3.5.0");
            var Q34;
            Q34=sQuery(id+"F16.wireOp",VERTEX,"E32.3.8.0");
            var Q35;
            Q35=sQuery(id+"F16.wireOp",VERTEX,"E31.direction1.start");
            var Q36;
            Q36=sQuery(id+"F16.wireOp",VERTEX,"E32.3.4.0");
            var Q37;
            Q37=sQuery(id+"F16.wireOp",VERTEX,"E31.direction1.end");
            var Q38;
            Q38=sQuery(id+"F16.wireOp",VERTEX,"E32.3.7.0");
            var Q39;
            Q39=sQuery(id+"F16.wireOp",VERTEX,"E32.3.3.0");
            var Q40;
            Q40=sQuery(id+"F16.wireOp",VERTEX,"E32.3.6.0");
            var Q41;
            Q41=sQuery(id+"F16.wireOp",VERTEX,"E31.2.0.3");
            var Q42;
            Q42=sQuery(id+"F16.wireOp",VERTEX,"E29.3.0.6");
            var Q43;
            Q43=sQuery(id+"F16.wireOp",VERTEX,"E29.5.0.6");
            var Q44;
            Q44=sQuery(id+"F16.wireOp",VERTEX,"E29.4.0.6");
            var Q45;
            Q45=sQuery(id+"F16.wireOp",VERTEX,"E29.6.0.6");
            var Q46;
            Q46=sQuery(id+"F16.wireOp",VERTEX,"E29.7.0.6");
            var Q47;
            Q47=sQuery(id+"F16.wireOp",VERTEX,"E28.6.0.0");
            var Q48;
            Q48=sQuery(id+"F16.wireOp",VERTEX,"E29.1.0.6");
            var Q49;
            Q49=sQuery(id+"F16.wireOp",VERTEX,"E29.2.0.6");
            var Q50;
            Q50=sQuery(id+"F16.wireOp",VERTEX,"E29.5.0.5");
            var Q51;
            Q51=sQuery(id+"F16.wireOp",VERTEX,"E29.3.0.5");
            var Q52;
            Q52=sQuery(id+"F16.wireOp",VERTEX,"E29.4.0.5");
            var Q53;
            Q53=sQuery(id+"F16.wireOp",VERTEX,"E29.2.0.5");
            var Q54;
            Q54=sQuery(id+"F16.wireOp",VERTEX,"E29.6.0.5");
            var Q55;
            Q55=sQuery(id+"F16.wireOp",VERTEX,"E28.5.0.0");
            var Q56;
            Q56=sQuery(id+"F16.wireOp",VERTEX,"E29.1.0.5");
            var Q57;
            Q57=sQuery(id+"F16.wireOp",VERTEX,"E28.3.0.0");
            var Q58;
            Q58=sQuery(id+"F16.wireOp",VERTEX,"E29.1.0.3");
            var Q59;
            Q59=sQuery(id+"F16.wireOp",VERTEX,"E29.2.0.3");
            var Q60;
            Q60=sQuery(id+"F16.wireOp",VERTEX,"E29.3.0.3");
            var Q61;
            Q61=sQuery(id+"F16.wireOp",VERTEX,"E29.4.0.3");
            var Q62;
            Q62=sQuery(id+"F16.wireOp",VERTEX,"E29.1.0.4");
            var Q63;
            Q63=sQuery(id+"F16.wireOp",VERTEX,"E29.4.0.4");
            var Q64;
            Q64=sQuery(id+"F16.wireOp",VERTEX,"E29.2.0.4");
            var Q65;
            Q65=sQuery(id+"F16.wireOp",VERTEX,"E28.4.0.0");
            var Q66;
            Q66=sQuery(id+"F16.wireOp",VERTEX,"E29.5.0.4");
            var Q67;
            Q67=sQuery(id+"F16.wireOp",VERTEX,"E29.3.0.4");
            var Q68;
            Q68=sQuery(id+"F16.wireOp",VERTEX,"E29.2.0.2");
            var Q69;
            Q69=sQuery(id+"F16.wireOp",VERTEX,"E29.3.0.2");
            var Q70;
            Q70=sQuery(id+"F16.wireOp",VERTEX,"E29.2.0.1");
            var Q71;
            Q71=sQuery(id+"F16.wireOp",VERTEX,"E28.direction1.end");
            var Q72;
            Q72=sQuery(id+"F16.wireOp",VERTEX,"E28.direction1.start");
            var Q73;
            Q73=sQuery(id+"F16.wireOp",VERTEX,"E28.2.0.0");
            var Q74;
            Q74=sQuery(id+"F16.wireOp",VERTEX,"E29.direction1.end");
            var Q75;
            Q75=sQuery(id+"F16.wireOp",VERTEX,"E29.1.0.1");
            var Q76;
            Q76=sQuery(id+"F16.wireOp",VERTEX,"E29.1.0.2");
            var Q77;
            Q77=makeQuery(id+"F1.opExtrude","SWEPT_BODY",BODY,{"disambiguationData":[OSD([sQuery(id+"F0.wireOp",EDGE,"E1.bottom"),sQuery(id+"F0.wireOp",EDGE,"E1.top"),sQuery(id+"F0.wireOp",EDGE,"E1.left"),sQuery(id+"F0.wireOp",EDGE,"E1.right"),sQuery(id+"F0.wireOp",EDGE,"E2"),sQuery(id+"F0.wireOp",EDGE,"E3"),sQuery(id+"F0.wireOp",EDGE,"E4"),sQuery(id+"F0.wireOp",EDGE,"E5"),sQuery(id+"F0.wireOp",EDGE,"E6"),sQuery(id+"F0.wireOp",EDGE,"E7"),sQuery(id+"F0.wireOp",EDGE,"E8"),sQuery(id+"F0.wireOp",EDGE,"E9.MirrorCS"),sQuery(id+"F0.wireOp",EDGE,"E10.MirrorCS"),sQuery(id+"F0.wireOp",EDGE,"E11.MirrorCS"),sQuery(id+"F0.wireOp",EDGE,"E13.trimOffspring"),sQuery(id+"F0.wireOp",EDGE,"E14.trimOffspring"),sQuery(id+"F0.wireOp",EDGE,"E16.trimOffspring"),sQuery(id+"F0.wireOp",EDGE,"E17.trimOffspring"),sQuery(id+"F0.wireOp",EDGE,"E20"),sQuery(id+"F0.wireOp",EDGE,"E21"),sQuery(id+"F0.wireOp",EDGE,"E23"),sQuery(id+"F0.wireOp",EDGE,"E24.trimOffspring")])]});
            var Q78;
            Q78=makeQuery(id+"F2.opExtrude","SWEPT_BODY",BODY,{"disambiguationData":[OSD([sQuery(id+"F0.wireOp",EDGE,"E26.1.0.0"),sQuery(id+"F0.wireOp",EDGE,"E26.1.0.1"),sQuery(id+"F0.wireOp",EDGE,"E26.1.0.5"),sQuery(id+"F0.wireOp",EDGE,"E26.1.0.9"),sQuery(id+"F0.wireOp",EDGE,"E26.1.0.10"),sQuery(id+"F0.wireOp",EDGE,"E26.1.0.11"),sQuery(id+"F0.wireOp",EDGE,"E26.1.0.14"),sQuery(id+"F0.wireOp",EDGE,"E26.1.0.15"),sQuery(id+"F0.wireOp",EDGE,"E26.1.0.16"),sQuery(id+"F0.wireOp",EDGE,"E26.1.0.17"),sQuery(id+"F0.wireOp",EDGE,"E26.1.0.18"),sQuery(id+"F0.wireOp",EDGE,"E26.1.0.19"),sQuery(id+"F0.wireOp",EDGE,"E26.1.0.20"),sQuery(id+"F0.wireOp",EDGE,"E26.1.0.21"),sQuery(id+"F0.wireOp",EDGE,"E26.1.0.22"),sQuery(id+"F0.wireOp",EDGE,"E26.1.0.23"),sQuery(id+"F0.wireOp",EDGE,"E26.1.0.24"),sQuery(id+"F0.wireOp",EDGE,"E26.1.0.25"),sQuery(id+"F0.wireOp",EDGE,"E26.1.0.26"),sQuery(id+"F0.wireOp",EDGE,"E26.1.0.27"),sQuery(id+"F0.wireOp",EDGE,"E26.1.0.28"),sQuery(id+"F0.wireOp",EDGE,"E26.1.0.29")])]});
            var Q79;
            Q79=makeQuery(id+"F3.opExtrude","SWEPT_BODY",BODY,{"disambiguationData":[OSD([sQuery(id+"F0.wireOp",EDGE,"E26.2.0.0"),sQuery(id+"F0.wireOp",EDGE,"E26.2.0.1"),sQuery(id+"F0.wireOp",EDGE,"E26.2.0.5"),sQuery(id+"F0.wireOp",EDGE,"E26.2.0.9"),sQuery(id+"F0.wireOp",EDGE,"E26.2.0.10"),sQuery(id+"F0.wireOp",EDGE,"E26.2.0.11"),sQuery(id+"F0.wireOp",EDGE,"E26.2.0.14"),sQuery(id+"F0.wireOp",EDGE,"E26.2.0.15"),sQuery(id+"F0.wireOp",EDGE,"E26.2.0.16"),sQuery(id+"F0.wireOp",EDGE,"E26.2.0.17"),sQuery(id+"F0.wireOp",EDGE,"E26.2.0.18"),sQuery(id+"F0.wireOp",EDGE,"E26.2.0.19"),sQuery(id+"F0.wireOp",EDGE,"E26.2.0.20"),sQuery(id+"F0.wireOp",EDGE,"E26.2.0.21"),sQuery(id+"F0.wireOp",EDGE,"E26.2.0.22"),sQuery(id+"F0.wireOp",EDGE,"E26.2.0.23"),sQuery(id+"F0.wireOp",EDGE,"E26.2.0.24"),sQuery(id+"F0.wireOp",EDGE,"E26.2.0.25"),sQuery(id+"F0.wireOp",EDGE,"E26.2.0.26"),sQuery(id+"F0.wireOp",EDGE,"E26.2.0.27"),sQuery(id+"F0.wireOp",EDGE,"E26.2.0.28"),sQuery(id+"F0.wireOp",EDGE,"E26.2.0.29")])]});
            var Q80;
            Q80=makeQuery(id+"F4.opExtrude","SWEPT_BODY",BODY,{"disambiguationData":[OSD([sQuery(id+"F0.wireOp",EDGE,"E26.3.0.0"),sQuery(id+"F0.wireOp",EDGE,"E26.3.0.1"),sQuery(id+"F0.wireOp",EDGE,"E26.3.0.5"),sQuery(id+"F0.wireOp",EDGE,"E26.3.0.9"),sQuery(id+"F0.wireOp",EDGE,"E26.3.0.10"),sQuery(id+"F0.wireOp",EDGE,"E26.3.0.11"),sQuery(id+"F0.wireOp",EDGE,"E26.3.0.14"),sQuery(id+"F0.wireOp",EDGE,"E26.3.0.15"),sQuery(id+"F0.wireOp",EDGE,"E26.3.0.16"),sQuery(id+"F0.wireOp",EDGE,"E26.3.0.17"),sQuery(id+"F0.wireOp",EDGE,"E26.3.0.18"),sQuery(id+"F0.wireOp",EDGE,"E26.3.0.19"),sQuery(id+"F0.wireOp",EDGE,"E26.3.0.20"),sQuery(id+"F0.wireOp",EDGE,"E26.3.0.21"),sQuery(id+"F0.wireOp",EDGE,"E26.3.0.22"),sQuery(id+"F0.wireOp",EDGE,"E26.3.0.23"),sQuery(id+"F0.wireOp",EDGE,"E26.3.0.24"),sQuery(id+"F0.wireOp",EDGE,"E26.3.0.25"),sQuery(id+"F0.wireOp",EDGE,"E26.3.0.26"),sQuery(id+"F0.wireOp",EDGE,"E26.3.0.27"),sQuery(id+"F0.wireOp",EDGE,"E26.3.0.28"),sQuery(id+"F0.wireOp",EDGE,"E26.3.0.29")])]});
            var Q81;
            Q81=makeQuery(id+"F5.opExtrude","SWEPT_BODY",BODY,{"disambiguationData":[OSD([sQuery(id+"F0.wireOp",EDGE,"E26.4.0.0"),sQuery(id+"F0.wireOp",EDGE,"E26.4.0.1"),sQuery(id+"F0.wireOp",EDGE,"E26.4.0.5"),sQuery(id+"F0.wireOp",EDGE,"E26.4.0.9"),sQuery(id+"F0.wireOp",EDGE,"E26.4.0.10"),sQuery(id+"F0.wireOp",EDGE,"E26.4.0.11"),sQuery(id+"F0.wireOp",EDGE,"E26.4.0.14"),sQuery(id+"F0.wireOp",EDGE,"E26.4.0.15"),sQuery(id+"F0.wireOp",EDGE,"E26.4.0.16"),sQuery(id+"F0.wireOp",EDGE,"E26.4.0.17"),sQuery(id+"F0.wireOp",EDGE,"E26.4.0.18"),sQuery(id+"F0.wireOp",EDGE,"E26.4.0.19"),sQuery(id+"F0.wireOp",EDGE,"E26.4.0.20"),sQuery(id+"F0.wireOp",EDGE,"E26.4.0.21"),sQuery(id+"F0.wireOp",EDGE,"E26.4.0.22"),sQuery(id+"F0.wireOp",EDGE,"E26.4.0.23"),sQuery(id+"F0.wireOp",EDGE,"E26.4.0.24"),sQuery(id+"F0.wireOp",EDGE,"E26.4.0.25"),sQuery(id+"F0.wireOp",EDGE,"E26.4.0.26"),sQuery(id+"F0.wireOp",EDGE,"E26.4.0.27"),sQuery(id+"F0.wireOp",EDGE,"E26.4.0.28"),sQuery(id+"F0.wireOp",EDGE,"E26.4.0.29")])]});
            var Q82;
            Q82=makeQuery(id+"F6.opExtrude","SWEPT_BODY",BODY,{"disambiguationData":[OSD([sQuery(id+"F0.wireOp",EDGE,"E26.5.0.0"),sQuery(id+"F0.wireOp",EDGE,"E26.5.0.1"),sQuery(id+"F0.wireOp",EDGE,"E26.5.0.5"),sQuery(id+"F0.wireOp",EDGE,"E26.5.0.9"),sQuery(id+"F0.wireOp",EDGE,"E26.5.0.10"),sQuery(id+"F0.wireOp",EDGE,"E26.5.0.11"),sQuery(id+"F0.wireOp",EDGE,"E26.5.0.14"),sQuery(id+"F0.wireOp",EDGE,"E26.5.0.15"),sQuery(id+"F0.wireOp",EDGE,"E26.5.0.16"),sQuery(id+"F0.wireOp",EDGE,"E26.5.0.17"),sQuery(id+"F0.wireOp",EDGE,"E26.5.0.18"),sQuery(id+"F0.wireOp",EDGE,"E26.5.0.19"),sQuery(id+"F0.wireOp",EDGE,"E26.5.0.20"),sQuery(id+"F0.wireOp",EDGE,"E26.5.0.21"),sQuery(id+"F0.wireOp",EDGE,"E26.5.0.22"),sQuery(id+"F0.wireOp",EDGE,"E26.5.0.23"),sQuery(id+"F0.wireOp",EDGE,"E26.5.0.24"),sQuery(id+"F0.wireOp",EDGE,"E26.5.0.25"),sQuery(id+"F0.wireOp",EDGE,"E26.5.0.26"),sQuery(id+"F0.wireOp",EDGE,"E26.5.0.27"),sQuery(id+"F0.wireOp",EDGE,"E26.5.0.28"),sQuery(id+"F0.wireOp",EDGE,"E26.5.0.29")])]});
            var Q83;
            Q83=makeQuery(id+"F7.opExtrude","SWEPT_BODY",BODY,{"disambiguationData":[OSD([sQuery(id+"F0.wireOp",EDGE,"E26.6.0.0"),sQuery(id+"F0.wireOp",EDGE,"E26.6.0.1"),sQuery(id+"F0.wireOp",EDGE,"E26.6.0.5"),sQuery(id+"F0.wireOp",EDGE,"E26.6.0.9"),sQuery(id+"F0.wireOp",EDGE,"E26.6.0.10"),sQuery(id+"F0.wireOp",EDGE,"E26.6.0.11"),sQuery(id+"F0.wireOp",EDGE,"E26.6.0.14"),sQuery(id+"F0.wireOp",EDGE,"E26.6.0.15"),sQuery(id+"F0.wireOp",EDGE,"E26.6.0.16"),sQuery(id+"F0.wireOp",EDGE,"E26.6.0.17"),sQuery(id+"F0.wireOp",EDGE,"E26.6.0.18"),sQuery(id+"F0.wireOp",EDGE,"E26.6.0.19"),sQuery(id+"F0.wireOp",EDGE,"E26.6.0.20"),sQuery(id+"F0.wireOp",EDGE,"E26.6.0.21"),sQuery(id+"F0.wireOp",EDGE,"E26.6.0.22"),sQuery(id+"F0.wireOp",EDGE,"E26.6.0.23"),sQuery(id+"F0.wireOp",EDGE,"E26.6.0.24"),sQuery(id+"F0.wireOp",EDGE,"E26.6.0.25"),sQuery(id+"F0.wireOp",EDGE,"E26.6.0.26"),sQuery(id+"F0.wireOp",EDGE,"E26.6.0.27"),sQuery(id+"F0.wireOp",EDGE,"E26.6.0.28"),sQuery(id+"F0.wireOp",EDGE,"E26.6.0.29")])]});
            var Q84;
            Q84=makeQuery(id+"F8.opExtrude","SWEPT_BODY",BODY,{"disambiguationData":[OSD([sQuery(id+"F0.wireOp",EDGE,"E26.7.0.0"),sQuery(id+"F0.wireOp",EDGE,"E26.7.0.1"),sQuery(id+"F0.wireOp",EDGE,"E26.7.0.5"),sQuery(id+"F0.wireOp",EDGE,"E26.7.0.9"),sQuery(id+"F0.wireOp",EDGE,"E26.7.0.10"),sQuery(id+"F0.wireOp",EDGE,"E26.7.0.11"),sQuery(id+"F0.wireOp",EDGE,"E26.7.0.14"),sQuery(id+"F0.wireOp",EDGE,"E26.7.0.15"),sQuery(id+"F0.wireOp",EDGE,"E26.7.0.16"),sQuery(id+"F0.wireOp",EDGE,"E26.7.0.17"),sQuery(id+"F0.wireOp",EDGE,"E26.7.0.18"),sQuery(id+"F0.wireOp",EDGE,"E26.7.0.19"),sQuery(id+"F0.wireOp",EDGE,"E26.7.0.20"),sQuery(id+"F0.wireOp",EDGE,"E26.7.0.21"),sQuery(id+"F0.wireOp",EDGE,"E26.7.0.22"),sQuery(id+"F0.wireOp",EDGE,"E26.7.0.23"),sQuery(id+"F0.wireOp",EDGE,"E26.7.0.24"),sQuery(id+"F0.wireOp",EDGE,"E26.7.0.25"),sQuery(id+"F0.wireOp",EDGE,"E26.7.0.26"),sQuery(id+"F0.wireOp",EDGE,"E26.7.0.27"),sQuery(id+"F0.wireOp",EDGE,"E26.7.0.28"),sQuery(id+"F0.wireOp",EDGE,"E26.7.0.29")])]});
            var Q85;
            Q85=makeQuery(id+"F9.opExtrude","SWEPT_BODY",BODY,{"disambiguationData":[OSD([sQuery(id+"F0.wireOp",EDGE,"E26.8.0.0"),sQuery(id+"F0.wireOp",EDGE,"E26.8.0.1"),sQuery(id+"F0.wireOp",EDGE,"E26.8.0.5"),sQuery(id+"F0.wireOp",EDGE,"E26.8.0.9"),sQuery(id+"F0.wireOp",EDGE,"E26.8.0.10"),sQuery(id+"F0.wireOp",EDGE,"E26.8.0.11"),sQuery(id+"F0.wireOp",EDGE,"E26.8.0.14"),sQuery(id+"F0.wireOp",EDGE,"E26.8.0.15"),sQuery(id+"F0.wireOp",EDGE,"E26.8.0.16"),sQuery(id+"F0.wireOp",EDGE,"E26.8.0.17"),sQuery(id+"F0.wireOp",EDGE,"E26.8.0.18"),sQuery(id+"F0.wireOp",EDGE,"E26.8.0.19"),sQuery(id+"F0.wireOp",EDGE,"E26.8.0.20"),sQuery(id+"F0.wireOp",EDGE,"E26.8.0.21"),sQuery(id+"F0.wireOp",EDGE,"E26.8.0.22"),sQuery(id+"F0.wireOp",EDGE,"E26.8.0.23"),sQuery(id+"F0.wireOp",EDGE,"E26.8.0.24"),sQuery(id+"F0.wireOp",EDGE,"E26.8.0.25"),sQuery(id+"F0.wireOp",EDGE,"E26.8.0.26"),sQuery(id+"F0.wireOp",EDGE,"E26.8.0.27"),sQuery(id+"F0.wireOp",EDGE,"E26.8.0.28"),sQuery(id+"F0.wireOp",EDGE,"E26.8.0.29")])]});
            var Q86;
            Q86=makeQuery(id+"F10.opExtrude","SWEPT_BODY",BODY,{"disambiguationData":[OSD([sQuery(id+"F0.wireOp",EDGE,"E26.9.0.0"),sQuery(id+"F0.wireOp",EDGE,"E26.9.0.1"),sQuery(id+"F0.wireOp",EDGE,"E26.9.0.5"),sQuery(id+"F0.wireOp",EDGE,"E26.9.0.9"),sQuery(id+"F0.wireOp",EDGE,"E26.9.0.10"),sQuery(id+"F0.wireOp",EDGE,"E26.9.0.11"),sQuery(id+"F0.wireOp",EDGE,"E26.9.0.14"),sQuery(id+"F0.wireOp",EDGE,"E26.9.0.15"),sQuery(id+"F0.wireOp",EDGE,"E26.9.0.16"),sQuery(id+"F0.wireOp",EDGE,"E26.9.0.17"),sQuery(id+"F0.wireOp",EDGE,"E26.9.0.18"),sQuery(id+"F0.wireOp",EDGE,"E26.9.0.19"),sQuery(id+"F0.wireOp",EDGE,"E26.9.0.20"),sQuery(id+"F0.wireOp",EDGE,"E26.9.0.21"),sQuery(id+"F0.wireOp",EDGE,"E26.9.0.22"),sQuery(id+"F0.wireOp",EDGE,"E26.9.0.23"),sQuery(id+"F0.wireOp",EDGE,"E26.9.0.24"),sQuery(id+"F0.wireOp",EDGE,"E26.9.0.25"),sQuery(id+"F0.wireOp",EDGE,"E26.9.0.26"),sQuery(id+"F0.wireOp",EDGE,"E26.9.0.27"),sQuery(id+"F0.wireOp",EDGE,"E26.9.0.28"),sQuery(id+"F0.wireOp",EDGE,"E26.9.0.29")])]});
            var Q87;
            Q87=makeQuery(id+"F11.opExtrude","SWEPT_BODY",BODY,{"disambiguationData":[OSD([sQuery(id+"F0.wireOp",EDGE,"E26.10.0.0"),sQuery(id+"F0.wireOp",EDGE,"E26.10.0.1"),sQuery(id+"F0.wireOp",EDGE,"E26.10.0.5"),sQuery(id+"F0.wireOp",EDGE,"E26.10.0.9"),sQuery(id+"F0.wireOp",EDGE,"E26.10.0.10"),sQuery(id+"F0.wireOp",EDGE,"E26.10.0.11"),sQuery(id+"F0.wireOp",EDGE,"E26.10.0.14"),sQuery(id+"F0.wireOp",EDGE,"E26.10.0.15"),sQuery(id+"F0.wireOp",EDGE,"E26.10.0.16"),sQuery(id+"F0.wireOp",EDGE,"E26.10.0.17"),sQuery(id+"F0.wireOp",EDGE,"E26.10.0.18"),sQuery(id+"F0.wireOp",EDGE,"E26.10.0.19"),sQuery(id+"F0.wireOp",EDGE,"E26.10.0.20"),sQuery(id+"F0.wireOp",EDGE,"E26.10.0.21"),sQuery(id+"F0.wireOp",EDGE,"E26.10.0.22"),sQuery(id+"F0.wireOp",EDGE,"E26.10.0.23"),sQuery(id+"F0.wireOp",EDGE,"E26.10.0.24"),sQuery(id+"F0.wireOp",EDGE,"E26.10.0.25"),sQuery(id+"F0.wireOp",EDGE,"E26.10.0.26"),sQuery(id+"F0.wireOp",EDGE,"E26.10.0.27"),sQuery(id+"F0.wireOp",EDGE,"E26.10.0.28"),sQuery(id+"F0.wireOp",EDGE,"E26.10.0.29")])]});
            hole(context, id + "F17", {"style" : HoleStyle.C_BORE, "endStyle" : HoleEndStyle.THROUGH, "holeDiameter" : 3.5 * mm, "cBoreDiameter" : 6 * mm, "cBoreDepth" : 4.5 * mm, "majorDiameter" : 5 * mm, "isTappedThrough" : true, "tappedDepth" : 12 * mm, "tapClearance" : 3, "locations" : qUnion([Q0, Q1, Q2, Q3, Q4, Q5, Q6, Q7, Q8, Q9, Q10, Q11, Q12, Q13, Q14, Q15, Q16, Q17, Q18, Q19, Q20, Q21, Q22, Q23, Q24, Q25, Q26, Q27, Q28, Q29, Q30, Q31, Q32, Q33, Q34, Q35, Q36, Q37, Q38, Q39, Q40, Q41, Q42, Q43, Q44, Q45, Q46, Q47, Q48, Q49, Q50, Q51, Q52, Q53, Q54, Q55, Q56, Q57, Q58, Q59, Q60, Q61, Q62, Q63, Q64, Q65, Q66, Q67, Q68, Q69, Q70, Q71, Q72, Q73, Q74, Q75, Q76]), "scope" : qUnion([Q77, Q78, Q79, Q80, Q81, Q82, Q83, Q84, Q85, Q86, Q87])});
        }
        {
            var Q0;
            Q0=sQuery(id+"F16.wireOp",VERTEX,"E35.1.6.0");
            var Q1;
            Q1=sQuery(id+"F16.wireOp",VERTEX,"E34.1.0.1");
            var Q2;
            Q2=sQuery(id+"F16.wireOp",VERTEX,"E35.1.8.0");
            var Q3;
            Q3=sQuery(id+"F16.wireOp",VERTEX,"E35.1.5.0");
            var Q4;
            Q4=sQuery(id+"F16.wireOp",VERTEX,"E35.1.13.0");
            var Q5;
            Q5=sQuery(id+"F16.wireOp",VERTEX,"E35.1.9.0");
            var Q6;
            Q6=sQuery(id+"F16.wireOp",VERTEX,"E35.1.12.0");
            var Q7;
            Q7=sQuery(id+"F16.wireOp",VERTEX,"E35.1.4.0");
            var Q8;
            Q8=sQuery(id+"F16.wireOp",VERTEX,"E35.1.3.0");
            var Q9;
            Q9=sQuery(id+"F16.wireOp",VERTEX,"E35.1.7.0");
            var Q10;
            Q10=sQuery(id+"F16.wireOp",VERTEX,"E33.0.11.0");
            var Q11;
            Q11=sQuery(id+"F16.wireOp",VERTEX,"E34.2.0.1");
            var Q12;
            Q12=sQuery(id+"F16.wireOp",VERTEX,"E35.1.11.0");
            var Q13;
            Q13=sQuery(id+"F16.wireOp",VERTEX,"E35.1.10.0");
            var Q14;
            Q14=sQuery(id+"F16.wireOp",VERTEX,"E35.3.14.0");
            var Q15;
            Q15=sQuery(id+"F16.wireOp",VERTEX,"E35.3.16.0");
            var Q16;
            Q16=sQuery(id+"F16.wireOp",VERTEX,"E35.3.12.0");
            var Q17;
            Q17=sQuery(id+"F16.wireOp",VERTEX,"E35.3.6.0");
            var Q18;
            Q18=sQuery(id+"F16.wireOp",VERTEX,"E35.3.8.0");
            var Q19;
            Q19=sQuery(id+"F16.wireOp",VERTEX,"E35.3.11.0");
            var Q20;
            Q20=sQuery(id+"F16.wireOp",VERTEX,"E35.3.15.0");
            var Q21;
            Q21=sQuery(id+"F16.wireOp",VERTEX,"E35.3.10.0");
            var Q22;
            Q22=sQuery(id+"F16.wireOp",VERTEX,"E35.3.13.0");
            var Q23;
            Q23=sQuery(id+"F16.wireOp",VERTEX,"E35.3.4.0");
            var Q24;
            Q24=sQuery(id+"F16.wireOp",VERTEX,"E34.2.0.3");
            var Q25;
            Q25=sQuery(id+"F16.wireOp",VERTEX,"E34.1.0.3");
            var Q26;
            Q26=sQuery(id+"F16.wireOp",VERTEX,"E35.3.9.0");
            var Q27;
            Q27=sQuery(id+"F16.wireOp",VERTEX,"E35.3.3.0");
            var Q28;
            Q28=sQuery(id+"F16.wireOp",VERTEX,"E35.3.7.0");
            var Q29;
            Q29=sQuery(id+"F16.wireOp",VERTEX,"E33.0.12.0");
            var Q30;
            Q30=sQuery(id+"F16.wireOp",VERTEX,"E35.3.5.0");
            var Q31;
            Q31=sQuery(id+"F16.wireOp",VERTEX,"E35.2.13.0");
            var Q32;
            Q32=sQuery(id+"F16.wireOp",VERTEX,"E35.2.9.0");
            var Q33;
            Q33=sQuery(id+"F16.wireOp",VERTEX,"E35.2.3.0");
            var Q34;
            Q34=sQuery(id+"F16.wireOp",VERTEX,"E35.2.11.0");
            var Q35;
            Q35=sQuery(id+"F16.wireOp",VERTEX,"E35.2.5.0");
            var Q36;
            Q36=sQuery(id+"F16.wireOp",VERTEX,"E33.0.13.0");
            var Q37;
            Q37=sQuery(id+"F16.wireOp",VERTEX,"E35.2.7.0");
            var Q38;
            Q38=sQuery(id+"F16.wireOp",VERTEX,"E35.2.12.0");
            var Q39;
            Q39=sQuery(id+"F16.wireOp",VERTEX,"E35.2.16.0");
            var Q40;
            Q40=sQuery(id+"F16.wireOp",VERTEX,"E35.2.8.0");
            var Q41;
            Q41=sQuery(id+"F16.wireOp",VERTEX,"E35.2.15.0");
            var Q42;
            Q42=sQuery(id+"F16.wireOp",VERTEX,"E34.2.0.2");
            var Q43;
            Q43=sQuery(id+"F16.wireOp",VERTEX,"E34.1.0.2");
            var Q44;
            Q44=sQuery(id+"F16.wireOp",VERTEX,"E35.2.4.0");
            var Q45;
            Q45=sQuery(id+"F16.wireOp",VERTEX,"E35.2.14.0");
            var Q46;
            Q46=sQuery(id+"F16.wireOp",VERTEX,"E35.2.6.0");
            var Q47;
            Q47=sQuery(id+"F16.wireOp",VERTEX,"E35.2.10.0");
            var Q48;
            Q48=sQuery(id+"F16.wireOp",VERTEX,"E35.2.20.0");
            var Q49;
            Q49=sQuery(id+"F16.wireOp",VERTEX,"E35.2.21.0");
            var Q50;
            Q50=sQuery(id+"F16.wireOp",VERTEX,"E35.2.17.0");
            var Q51;
            Q51=sQuery(id+"F16.wireOp",VERTEX,"E35.2.18.0");
            var Q52;
            Q52=sQuery(id+"F16.wireOp",VERTEX,"E35.2.19.0");
            var Q53;
            Q53=makeQuery(id+"F11.opExtrude","SWEPT_BODY",BODY,{"disambiguationData":[OSD([sQuery(id+"F0.wireOp",EDGE,"E26.10.0.0"),sQuery(id+"F0.wireOp",EDGE,"E26.10.0.1"),sQuery(id+"F0.wireOp",EDGE,"E26.10.0.5"),sQuery(id+"F0.wireOp",EDGE,"E26.10.0.9"),sQuery(id+"F0.wireOp",EDGE,"E26.10.0.10"),sQuery(id+"F0.wireOp",EDGE,"E26.10.0.11"),sQuery(id+"F0.wireOp",EDGE,"E26.10.0.14"),sQuery(id+"F0.wireOp",EDGE,"E26.10.0.15"),sQuery(id+"F0.wireOp",EDGE,"E26.10.0.16"),sQuery(id+"F0.wireOp",EDGE,"E26.10.0.17"),sQuery(id+"F0.wireOp",EDGE,"E26.10.0.18"),sQuery(id+"F0.wireOp",EDGE,"E26.10.0.19"),sQuery(id+"F0.wireOp",EDGE,"E26.10.0.20"),sQuery(id+"F0.wireOp",EDGE,"E26.10.0.21"),sQuery(id+"F0.wireOp",EDGE,"E26.10.0.22"),sQuery(id+"F0.wireOp",EDGE,"E26.10.0.23"),sQuery(id+"F0.wireOp",EDGE,"E26.10.0.24"),sQuery(id+"F0.wireOp",EDGE,"E26.10.0.25"),sQuery(id+"F0.wireOp",EDGE,"E26.10.0.26"),sQuery(id+"F0.wireOp",EDGE,"E26.10.0.27"),sQuery(id+"F0.wireOp",EDGE,"E26.10.0.28"),sQuery(id+"F0.wireOp",EDGE,"E26.10.0.29")])]});
            var Q54;
            Q54=makeQuery(id+"F12.opExtrude","SWEPT_BODY",BODY,{"disambiguationData":[OSD([sQuery(id+"F0.wireOp",EDGE,"E26.11.0.0"),sQuery(id+"F0.wireOp",EDGE,"E26.11.0.1"),sQuery(id+"F0.wireOp",EDGE,"E26.11.0.5"),sQuery(id+"F0.wireOp",EDGE,"E26.11.0.9"),sQuery(id+"F0.wireOp",EDGE,"E26.11.0.10"),sQuery(id+"F0.wireOp",EDGE,"E26.11.0.11"),sQuery(id+"F0.wireOp",EDGE,"E26.11.0.14"),sQuery(id+"F0.wireOp",EDGE,"E26.11.0.15"),sQuery(id+"F0.wireOp",EDGE,"E26.11.0.16"),sQuery(id+"F0.wireOp",EDGE,"E26.11.0.17"),sQuery(id+"F0.wireOp",EDGE,"E26.11.0.18"),sQuery(id+"F0.wireOp",EDGE,"E26.11.0.19"),sQuery(id+"F0.wireOp",EDGE,"E26.11.0.20"),sQuery(id+"F0.wireOp",EDGE,"E26.11.0.21"),sQuery(id+"F0.wireOp",EDGE,"E26.11.0.22"),sQuery(id+"F0.wireOp",EDGE,"E26.11.0.23"),sQuery(id+"F0.wireOp",EDGE,"E26.11.0.24"),sQuery(id+"F0.wireOp",EDGE,"E26.11.0.25"),sQuery(id+"F0.wireOp",EDGE,"E26.11.0.26"),sQuery(id+"F0.wireOp",EDGE,"E26.11.0.27"),sQuery(id+"F0.wireOp",EDGE,"E26.11.0.28"),sQuery(id+"F0.wireOp",EDGE,"E26.11.0.29")])]});
            var Q55;
            Q55=makeQuery(id+"F13.opExtrude","SWEPT_BODY",BODY,{"disambiguationData":[OSD([sQuery(id+"F0.wireOp",EDGE,"E26.12.0.0"),sQuery(id+"F0.wireOp",EDGE,"E26.12.0.1"),sQuery(id+"F0.wireOp",EDGE,"E26.12.0.5"),sQuery(id+"F0.wireOp",EDGE,"E26.12.0.9"),sQuery(id+"F0.wireOp",EDGE,"E26.12.0.10"),sQuery(id+"F0.wireOp",EDGE,"E26.12.0.11"),sQuery(id+"F0.wireOp",EDGE,"E26.12.0.14"),sQuery(id+"F0.wireOp",EDGE,"E26.12.0.15"),sQuery(id+"F0.wireOp",EDGE,"E26.12.0.16"),sQuery(id+"F0.wireOp",EDGE,"E26.12.0.17"),sQuery(id+"F0.wireOp",EDGE,"E26.12.0.18"),sQuery(id+"F0.wireOp",EDGE,"E26.12.0.19"),sQuery(id+"F0.wireOp",EDGE,"E26.12.0.20"),sQuery(id+"F0.wireOp",EDGE,"E26.12.0.21"),sQuery(id+"F0.wireOp",EDGE,"E26.12.0.22"),sQuery(id+"F0.wireOp",EDGE,"E26.12.0.23"),sQuery(id+"F0.wireOp",EDGE,"E26.12.0.24"),sQuery(id+"F0.wireOp",EDGE,"E26.12.0.25"),sQuery(id+"F0.wireOp",EDGE,"E26.12.0.26"),sQuery(id+"F0.wireOp",EDGE,"E26.12.0.27"),sQuery(id+"F0.wireOp",EDGE,"E26.12.0.28"),sQuery(id+"F0.wireOp",EDGE,"E26.12.0.29")])]});
            var Q56;
            Q56=makeQuery(id+"F14.opExtrude","SWEPT_BODY",BODY,{"disambiguationData":[OSD([sQuery(id+"F0.wireOp",EDGE,"E26.13.0.0"),sQuery(id+"F0.wireOp",EDGE,"E26.13.0.1"),sQuery(id+"F0.wireOp",EDGE,"E26.13.0.5"),sQuery(id+"F0.wireOp",EDGE,"E26.13.0.9"),sQuery(id+"F0.wireOp",EDGE,"E26.13.0.10"),sQuery(id+"F0.wireOp",EDGE,"E26.13.0.11"),sQuery(id+"F0.wireOp",EDGE,"E26.13.0.14"),sQuery(id+"F0.wireOp",EDGE,"E26.13.0.15"),sQuery(id+"F0.wireOp",EDGE,"E26.13.0.16"),sQuery(id+"F0.wireOp",EDGE,"E26.13.0.17"),sQuery(id+"F0.wireOp",EDGE,"E26.13.0.18"),sQuery(id+"F0.wireOp",EDGE,"E26.13.0.19"),sQuery(id+"F0.wireOp",EDGE,"E26.13.0.20"),sQuery(id+"F0.wireOp",EDGE,"E26.13.0.21"),sQuery(id+"F0.wireOp",EDGE,"E26.13.0.22"),sQuery(id+"F0.wireOp",EDGE,"E26.13.0.23"),sQuery(id+"F0.wireOp",EDGE,"E26.13.0.24"),sQuery(id+"F0.wireOp",EDGE,"E26.13.0.25"),sQuery(id+"F0.wireOp",EDGE,"E26.13.0.26"),sQuery(id+"F0.wireOp",EDGE,"E26.13.0.27"),sQuery(id+"F0.wireOp",EDGE,"E26.13.0.28"),sQuery(id+"F0.wireOp",EDGE,"E26.13.0.29")])]});
            hole(context, id + "F18", {"style" : HoleStyle.C_BORE, "endStyle" : HoleEndStyle.THROUGH, "holeDiameter" : 3.5 * mm, "cBoreDiameter" : 6 * mm, "cBoreDepth" : 4.5 * mm, "majorDiameter" : 5 * mm, "isTappedThrough" : true, "tappedDepth" : 12 * mm, "tapClearance" : 3, "locations" : qUnion([Q0, Q1, Q2, Q3, Q4, Q5, Q6, Q7, Q8, Q9, Q10, Q11, Q12, Q13, Q14, Q15, Q16, Q17, Q18, Q19, Q20, Q21, Q22, Q23, Q24, Q25, Q26, Q27, Q28, Q29, Q30, Q31, Q32, Q33, Q34, Q35, Q36, Q37, Q38, Q39, Q40, Q41, Q42, Q43, Q44, Q45, Q46, Q47, Q48, Q49, Q50, Q51, Q52]), "scope" : qUnion([Q53, Q54, Q55, Q56])});
        }
        {
            var Q0;
            Q0=sQuery(id+"F16.wireOp",VERTEX,"E35.0.47.0");
            var Q1;
            Q1=sQuery(id+"F16.wireOp",VERTEX,"E35.0.39.0");
            var Q2;
            Q2=sQuery(id+"F16.wireOp",VERTEX,"E35.0.33.0");
            var Q3;
            Q3=sQuery(id+"F16.wireOp",VERTEX,"E35.0.43.0");
            var Q4;
            Q4=sQuery(id+"F16.wireOp",VERTEX,"E35.0.36.0");
            var Q5;
            Q5=sQuery(id+"F16.wireOp",VERTEX,"E35.0.35.0");
            var Q6;
            Q6=sQuery(id+"F16.wireOp",VERTEX,"E35.0.28.0");
            var Q7;
            Q7=sQuery(id+"F16.wireOp",VERTEX,"E35.0.44.0");
            var Q8;
            Q8=sQuery(id+"F16.wireOp",VERTEX,"E35.0.40.0");
            var Q9;
            Q9=sQuery(id+"F16.wireOp",VERTEX,"E35.0.31.0");
            var Q10;
            Q10=sQuery(id+"F16.wireOp",VERTEX,"E35.0.45.0");
            var Q11;
            Q11=sQuery(id+"F16.wireOp",VERTEX,"E35.0.30.0");
            var Q12;
            Q12=sQuery(id+"F16.wireOp",VERTEX,"E35.0.38.0");
            var Q13;
            Q13=sQuery(id+"F16.wireOp",VERTEX,"E35.0.46.0");
            var Q14;
            Q14=sQuery(id+"F16.wireOp",VERTEX,"E35.0.34.0");
            var Q15;
            Q15=sQuery(id+"F16.wireOp",VERTEX,"E35.0.42.0");
            var Q16;
            Q16=sQuery(id+"F16.wireOp",VERTEX,"E35.0.41.0");
            var Q17;
            Q17=sQuery(id+"F16.wireOp",VERTEX,"E35.0.27.0");
            var Q18;
            Q18=sQuery(id+"F16.wireOp",VERTEX,"E35.0.37.0");
            var Q19;
            Q19=sQuery(id+"F16.wireOp",VERTEX,"E35.0.29.0");
            var Q20;
            Q20=sQuery(id+"F16.wireOp",VERTEX,"E35.0.49.0");
            var Q21;
            Q21=sQuery(id+"F16.wireOp",VERTEX,"E35.0.32.0");
            var Q22;
            Q22=sQuery(id+"F16.wireOp",VERTEX,"E35.0.48.0");
            var Q23;
            Q23=sQuery(id+"F16.wireOp",VERTEX,"E35.0.26.0");
            var Q24;
            Q24=sQuery(id+"F16.wireOp",VERTEX,"E35.0.10.0");
            var Q25;
            Q25=sQuery(id+"F16.wireOp",VERTEX,"E33.0.14.0");
            var Q26;
            Q26=sQuery(id+"F16.wireOp",VERTEX,"E35.0.25.0");
            var Q27;
            Q27=sQuery(id+"F16.wireOp",VERTEX,"E35.0.6.0");
            var Q28;
            Q28=sQuery(id+"F16.wireOp",VERTEX,"E35.0.9.0");
            var Q29;
            Q29=sQuery(id+"F16.wireOp",VERTEX,"E35.0.13.0");
            var Q30;
            Q30=sQuery(id+"F16.wireOp",VERTEX,"E35.0.5.0");
            var Q31;
            Q31=sQuery(id+"F16.wireOp",VERTEX,"E35.0.17.0");
            var Q32;
            Q32=sQuery(id+"F16.wireOp",VERTEX,"E34.1.0.0");
            var Q33;
            Q33=sQuery(id+"F16.wireOp",VERTEX,"E35.0.4.0");
            var Q34;
            Q34=sQuery(id+"F16.wireOp",VERTEX,"E35.0.12.0");
            var Q35;
            Q35=sQuery(id+"F16.wireOp",VERTEX,"E35.0.24.0");
            var Q36;
            Q36=sQuery(id+"F16.wireOp",VERTEX,"E35.0.16.0");
            var Q37;
            Q37=sQuery(id+"F16.wireOp",VERTEX,"E35.0.8.0");
            var Q38;
            Q38=sQuery(id+"F16.wireOp",VERTEX,"E34.2.0.0");
            var Q39;
            Q39=sQuery(id+"F16.wireOp",VERTEX,"E35.0.18.0");
            var Q40;
            Q40=sQuery(id+"F16.wireOp",VERTEX,"E35.0.21.0");
            var Q41;
            Q41=sQuery(id+"F16.wireOp",VERTEX,"E35.0.19.0");
            var Q42;
            Q42=sQuery(id+"F16.wireOp",VERTEX,"E35.0.23.0");
            var Q43;
            Q43=sQuery(id+"F16.wireOp",VERTEX,"E35.0.7.0");
            var Q44;
            Q44=sQuery(id+"F16.wireOp",VERTEX,"E35.0.3.0");
            var Q45;
            Q45=sQuery(id+"F16.wireOp",VERTEX,"E35.0.15.0");
            var Q46;
            Q46=sQuery(id+"F16.wireOp",VERTEX,"E35.0.20.0");
            var Q47;
            Q47=sQuery(id+"F16.wireOp",VERTEX,"E35.0.11.0");
            var Q48;
            Q48=sQuery(id+"F16.wireOp",VERTEX,"E35.0.22.0");
            var Q49;
            Q49=sQuery(id+"F16.wireOp",VERTEX,"E35.0.14.0");
            var Q50;
            Q50=makeQuery(id+"F15.opExtrude","SWEPT_BODY",BODY,{"disambiguationData":[OSD([sQuery(id+"F0.wireOp",EDGE,"E26.14.0.0"),sQuery(id+"F0.wireOp",EDGE,"E26.14.0.1"),sQuery(id+"F0.wireOp",EDGE,"E26.14.0.5"),sQuery(id+"F0.wireOp",EDGE,"E26.14.0.9"),sQuery(id+"F0.wireOp",EDGE,"E26.14.0.10"),sQuery(id+"F0.wireOp",EDGE,"E26.14.0.11"),sQuery(id+"F0.wireOp",EDGE,"E26.14.0.14"),sQuery(id+"F0.wireOp",EDGE,"E26.14.0.15"),sQuery(id+"F0.wireOp",EDGE,"E26.14.0.16"),sQuery(id+"F0.wireOp",EDGE,"E26.14.0.17"),sQuery(id+"F0.wireOp",EDGE,"E26.14.0.18"),sQuery(id+"F0.wireOp",EDGE,"E26.14.0.19"),sQuery(id+"F0.wireOp",EDGE,"E26.14.0.20"),sQuery(id+"F0.wireOp",EDGE,"E26.14.0.21"),sQuery(id+"F0.wireOp",EDGE,"E26.14.0.22"),sQuery(id+"F0.wireOp",EDGE,"E26.14.0.23"),sQuery(id+"F0.wireOp",EDGE,"E26.14.0.24"),sQuery(id+"F0.wireOp",EDGE,"E26.14.0.25"),sQuery(id+"F0.wireOp",EDGE,"E26.14.0.26"),sQuery(id+"F0.wireOp",EDGE,"E26.14.0.27"),sQuery(id+"F0.wireOp",EDGE,"E26.14.0.28"),sQuery(id+"F0.wireOp",EDGE,"E26.14.0.29")])]});
            hole(context, id + "F19", {"style" : HoleStyle.C_BORE, "endStyle" : HoleEndStyle.THROUGH, "holeDiameter" : 3.5 * mm, "cBoreDiameter" : 6 * mm, "cBoreDepth" : 4.5 * mm, "majorDiameter" : 5 * mm, "isTappedThrough" : true, "tappedDepth" : 12 * mm, "tapClearance" : 3, "locations" : qUnion([Q0, Q1, Q2, Q3, Q4, Q5, Q6, Q7, Q8, Q9, Q10, Q11, Q12, Q13, Q14, Q15, Q16, Q17, Q18, Q19, Q20, Q21, Q22, Q23, Q24, Q25, Q26, Q27, Q28, Q29, Q30, Q31, Q32, Q33, Q34, Q35, Q36, Q37, Q38, Q39, Q40, Q41, Q42, Q43, Q44, Q45, Q46, Q47, Q48, Q49]), "scope" : qUnion([Q50])});
        }
    });
